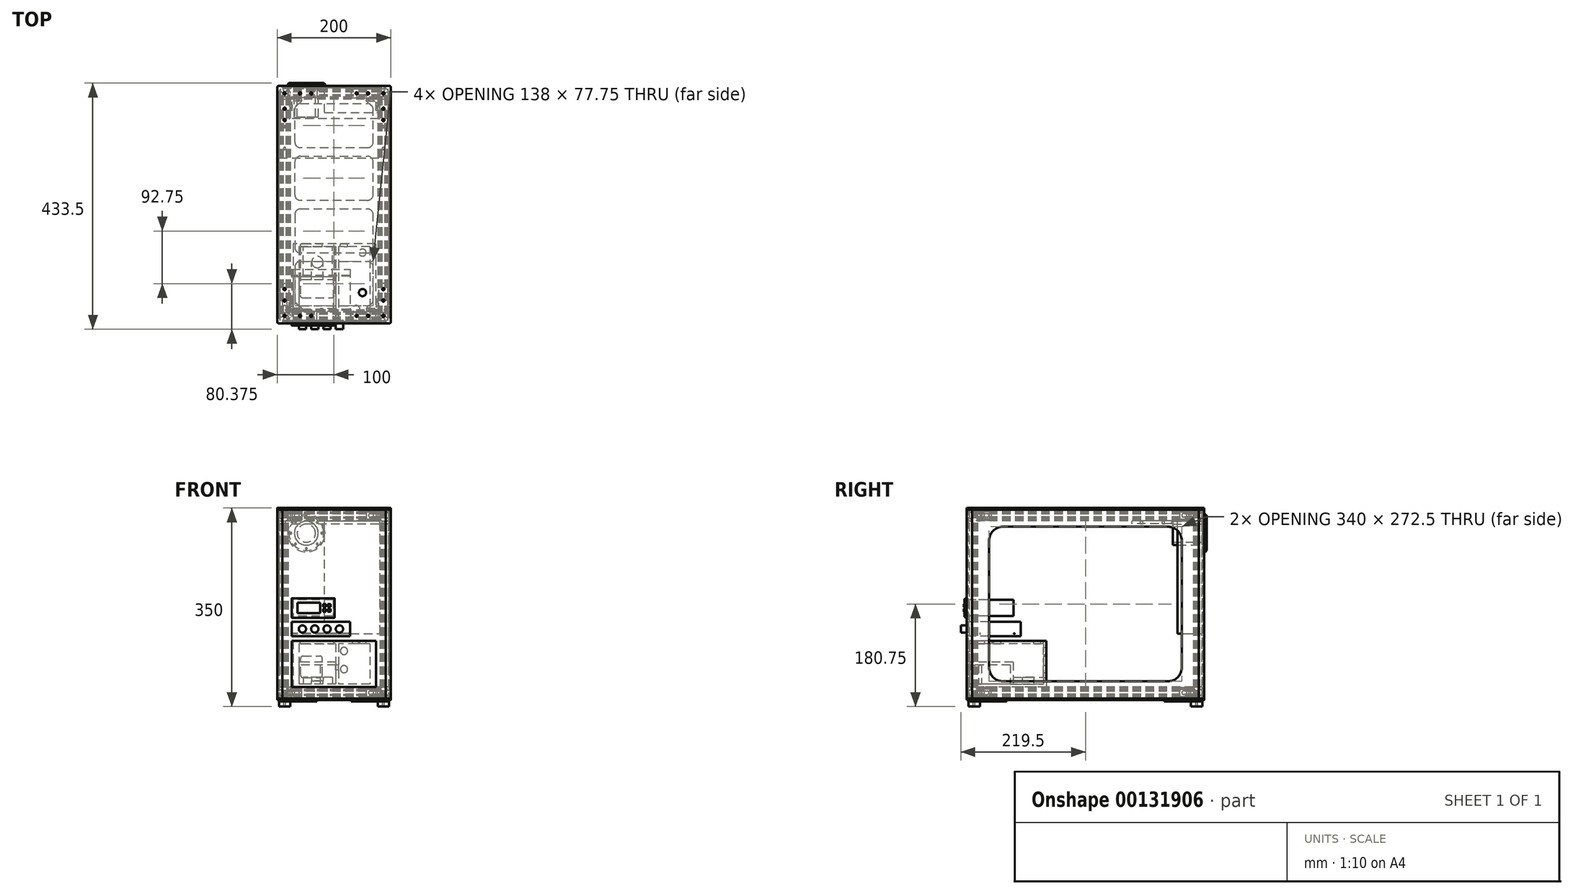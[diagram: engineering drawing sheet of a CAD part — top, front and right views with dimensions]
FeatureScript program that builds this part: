
annotation { "Feature Type Name" : "Feature", "Feature Type Description" : "" }
export const myFeature = defineFeature(function(context is Context, id is Id, definition is map)
    precondition{}
    {
        {
            var Q0;
            Q0=qCreatedBy(makeId("Front.planeOp"),FACE);
            var sketch = newSketch(context, id + "F0", { "sketchPlane" : qUnion([Q0])});
            skLineSegment(sketch, "E0.bottom", {"start": v(0, 0) * mm, "end": v(182, 0) * mm});
            skLineSegment(sketch, "E0.top", {"start": v(0, 332.5) * mm, "end": v(182, 332.5) * mm});
            skLineSegment(sketch, "E0.left", {"start": v(0, 0) * mm, "end": v(0, 332.5) * mm});
            skLineSegment(sketch, "E0.right", {"start": v(182, 0) * mm, "end": v(182, 332.5) * mm});
            skSolve(sketch);
        }
        {
            var Q0;
            Q0 = qSketchRegion(id + "F0", true);
            extrude(context, id + "F1", {"entities" : qUnion([Q0]), "oppositeDirection" : true, "depth" : 3 * mm});
        }
        {
            var Q0;
            Q0=makeQuery(id+"F1.opExtrude","SWEPT_FACE",FACE,{"disambiguationData":[OSD([sQuery(id+"F0.wireOp",EDGE,"E0.bottom")])]});
            var sketch = newSketch(context, id + "F2", { "sketchPlane" : qUnion([Q0])});
            skLineSegment(sketch, "E1.left", {"start": v(172, -3) * mm, "end": v(172, -11.56) * mm});
            skLineSegment(sketch, "E2", {"start": v(182, 0) * mm, "end": v(182, -3) * mm});
            skLineSegment(sketch, "E3", {"start": v(182, -3) * mm, "end": v(179.25, -3) * mm});
            skLineSegment(sketch, "E4", {"start": v(172, -19) * mm, "end": v(191, 0) * mm, "construction": true});
            skLineSegment(sketch, "E5", {"start": v(182, 0) * mm, "end": v(191, 0) * mm});
            skLineSegment(sketch, "E6", {"start": v(179.25, -3) * mm, "end": v(179.25, -4.5) * mm});
            skLineSegment(sketch, "E7", {"start": v(179.25, -4.5) * mm, "end": v(180.34, -4.5) * mm});
            skLineSegment(sketch, "E8", {"start": v(180.34, -4.5) * mm, "end": v(180.34, -8.25) * mm});
            skLineSegment(sketch, "E9", {"start": v(180.34, -8.25) * mm, "end": v(179.25, -8.25) * mm});
            skLineSegment(sketch, "E10", {"start": v(179.25, -8.25) * mm, "end": v(179.25, -10) * mm});
            skLineSegment(sketch, "E11", {"start": v(179.25, -10) * mm, "end": v(174.75, -10) * mm});
            skLineSegment(sketch, "E12", {"start": v(174.75, -10) * mm, "end": v(174.75, -8.25) * mm});
            skLineSegment(sketch, "E13", {"start": v(174.75, -8.25) * mm, "end": v(173.66, -8.25) * mm});
            skLineSegment(sketch, "E14", {"start": v(173.66, -8.25) * mm, "end": v(173.66, -4.5) * mm});
            skLineSegment(sketch, "E15", {"start": v(173.66, -4.5) * mm, "end": v(174.75, -4.5) * mm});
            skLineSegment(sketch, "E16", {"start": v(174.75, -4.5) * mm, "end": v(174.75, -3) * mm});
            skLineSegment(sketch, "E17", {"start": v(177, -10) * mm, "end": v(177, -3) * mm, "construction": true});
            skLineSegment(sketch, "E18.trimOffspring", {"start": v(174.75, -3) * mm, "end": v(172, -3) * mm});
            skArc(sketch, "E19", {"start": v(179.17, -11.83) * mm, "mid": v(177.27, -11.52) * mm, "end": v(176.36, -13.22) * mm});
            skArc(sketch, "E20", {"start": v(172, -11.56) * mm, "mid": v(173.6, -13.9) * mm, "end": v(176.36, -13.22) * mm});
            skLineSegment(sketch, "E21.MirrorCS", {"start": v(186.5, -16.25) * mm, "end": v(188, -16.25) * mm});
            skLineSegment(sketch, "E22.MirrorCS", {"start": v(181, -14) * mm, "end": v(188, -14) * mm, "construction": true});
            skLineSegment(sketch, "E23.MirrorCS", {"start": v(186.5, -11.75) * mm, "end": v(186.5, -10.66) * mm});
            skArc(sketch, "E24.MirrorCS", {"start": v(179.44, -19) * mm, "mid": v(177.1, -17.4) * mm, "end": v(177.78, -14.64) * mm});
            skLineSegment(sketch, "E25.MirrorCS", {"start": v(182.75, -10.66) * mm, "end": v(182.75, -11.75) * mm});
            skLineSegment(sketch, "E26.MirrorCS", {"start": v(182.75, -11.75) * mm, "end": v(181, -11.75) * mm});
            skLineSegment(sketch, "E27.MirrorCS", {"start": v(182.75, -17.34) * mm, "end": v(186.5, -17.34) * mm});
            skLineSegment(sketch, "E28.MirrorCS", {"start": v(186.5, -10.66) * mm, "end": v(182.75, -10.66) * mm});
            skLineSegment(sketch, "E29.MirrorCS", {"start": v(191, -9) * mm, "end": v(191, 0) * mm});
            skLineSegment(sketch, "E30.MirrorCS", {"start": v(181, -11.75) * mm, "end": v(181, -16.25) * mm});
            skLineSegment(sketch, "E31.MirrorCS", {"start": v(181, -16.25) * mm, "end": v(182.75, -16.25) * mm});
            skLineSegment(sketch, "E32.MirrorCS", {"start": v(188, -11.75) * mm, "end": v(186.5, -11.75) * mm});
            skLineSegment(sketch, "E33.MirrorCS", {"start": v(188, -19) * mm, "end": v(179.44, -19) * mm});
            skLineSegment(sketch, "E34.MirrorCS", {"start": v(191, -9) * mm, "end": v(188, -9) * mm});
            skLineSegment(sketch, "E35.MirrorCS", {"start": v(182.75, -16.25) * mm, "end": v(182.75, -17.34) * mm});
            skLineSegment(sketch, "E36.MirrorCS", {"start": v(188, -9) * mm, "end": v(188, -11.75) * mm});
            skLineSegment(sketch, "E37.MirrorCS", {"start": v(188, -16.25) * mm, "end": v(188, -19) * mm});
            skLineSegment(sketch, "E38.MirrorCS", {"start": v(186.5, -17.34) * mm, "end": v(186.5, -16.25) * mm});
            skArc(sketch, "E39.MirrorCS", {"start": v(179.17, -11.83) * mm, "mid": v(179.48, -13.73) * mm, "end": v(177.78, -14.64) * mm});
            skPoint(sketch, "E40.orphan", {"position": v(172, -19) * mm});
            skLineSegment(sketch, "E41.left", {"start": v(117.4, -37.11) * mm, "end": v(117.4, -45.67) * mm, "construction": true});
            skLineSegment(sketch, "E42", {"start": v(127.4, -34.11) * mm, "end": v(127.4, -37.11) * mm, "construction": true});
            skLineSegment(sketch, "E43", {"start": v(127.4, -37.11) * mm, "end": v(124.65, -37.11) * mm, "construction": true});
            skLineSegment(sketch, "E44", {"start": v(117.4, -53.11) * mm, "end": v(136.4, -34.11) * mm, "construction": true});
            skLineSegment(sketch, "E45", {"start": v(127.4, -34.11) * mm, "end": v(136.4, -34.11) * mm, "construction": true});
            skLineSegment(sketch, "E46", {"start": v(124.65, -37.11) * mm, "end": v(124.65, -38.61) * mm, "construction": true});
            skLineSegment(sketch, "E47", {"start": v(124.65, -38.61) * mm, "end": v(126.08, -38.61) * mm, "construction": true});
            skLineSegment(sketch, "E48", {"start": v(126.08, -38.61) * mm, "end": v(126.08, -42.36) * mm, "construction": true});
            skLineSegment(sketch, "E49", {"start": v(126.08, -42.36) * mm, "end": v(124.65, -42.36) * mm, "construction": true});
            skLineSegment(sketch, "E50", {"start": v(124.65, -42.36) * mm, "end": v(124.65, -44.11) * mm, "construction": true});
            skLineSegment(sketch, "E51", {"start": v(124.65, -44.11) * mm, "end": v(120.15, -44.11) * mm, "construction": true});
            skLineSegment(sketch, "E52", {"start": v(120.15, -44.11) * mm, "end": v(120.15, -42.36) * mm, "construction": true});
            skLineSegment(sketch, "E53", {"start": v(120.15, -42.36) * mm, "end": v(118.72, -42.36) * mm, "construction": true});
            skLineSegment(sketch, "E54", {"start": v(118.72, -42.36) * mm, "end": v(118.72, -38.61) * mm, "construction": true});
            skLineSegment(sketch, "E55", {"start": v(118.72, -38.61) * mm, "end": v(120.15, -38.61) * mm, "construction": true});
            skLineSegment(sketch, "E56", {"start": v(120.15, -38.61) * mm, "end": v(120.15, -37.11) * mm, "construction": true});
            skLineSegment(sketch, "E57", {"start": v(122.4, -44.11) * mm, "end": v(122.4, -37.11) * mm, "construction": true});
            skLineSegment(sketch, "E58.trimOffspring", {"start": v(120.15, -37.11) * mm, "end": v(117.4, -37.11) * mm, "construction": true});
            skArc(sketch, "E59", {"start": v(124.57, -45.95) * mm, "mid": v(122.67, -45.64) * mm, "end": v(121.76, -47.34) * mm, "construction": true});
            skArc(sketch, "E60", {"start": v(117.4, -45.67) * mm, "mid": v(119, -48) * mm, "end": v(121.76, -47.34) * mm, "construction": true});
            skLineSegment(sketch, "E61.MirrorCS", {"start": v(131.9, -50.36) * mm, "end": v(133.4, -50.36) * mm, "construction": true});
            skLineSegment(sketch, "E62.MirrorCS", {"start": v(126.4, -48.11) * mm, "end": v(133.4, -48.11) * mm, "construction": true});
            skLineSegment(sketch, "E63.MirrorCS", {"start": v(131.9, -45.86) * mm, "end": v(131.9, -44.44) * mm, "construction": true});
            skArc(sketch, "E64.MirrorCS", {"start": v(124.84, -53.11) * mm, "mid": v(122.5, -51.5) * mm, "end": v(123.18, -48.75) * mm, "construction": true});
            skLineSegment(sketch, "E65.MirrorCS", {"start": v(128.15, -44.44) * mm, "end": v(128.15, -45.86) * mm, "construction": true});
            skLineSegment(sketch, "E66.MirrorCS", {"start": v(128.15, -45.86) * mm, "end": v(126.4, -45.86) * mm, "construction": true});
            skLineSegment(sketch, "E67.MirrorCS", {"start": v(128.15, -51.8) * mm, "end": v(131.9, -51.8) * mm, "construction": true});
            skLineSegment(sketch, "E68.MirrorCS", {"start": v(131.9, -44.44) * mm, "end": v(128.15, -44.44) * mm, "construction": true});
            skLineSegment(sketch, "E69.MirrorCS", {"start": v(136.4, -43.11) * mm, "end": v(136.4, -34.11) * mm, "construction": true});
            skLineSegment(sketch, "E70.MirrorCS", {"start": v(126.4, -45.86) * mm, "end": v(126.4, -50.36) * mm, "construction": true});
            skLineSegment(sketch, "E71.MirrorCS", {"start": v(126.4, -50.36) * mm, "end": v(128.15, -50.36) * mm, "construction": true});
            skLineSegment(sketch, "E72.MirrorCS", {"start": v(133.4, -45.86) * mm, "end": v(131.9, -45.86) * mm, "construction": true});
            skLineSegment(sketch, "E73.MirrorCS", {"start": v(133.4, -53.11) * mm, "end": v(124.84, -53.11) * mm, "construction": true});
            skLineSegment(sketch, "E74.MirrorCS", {"start": v(136.4, -43.11) * mm, "end": v(133.4, -43.11) * mm, "construction": true});
            skLineSegment(sketch, "E75.MirrorCS", {"start": v(128.15, -50.36) * mm, "end": v(128.15, -51.8) * mm, "construction": true});
            skLineSegment(sketch, "E76.MirrorCS", {"start": v(133.4, -43.11) * mm, "end": v(133.4, -45.86) * mm, "construction": true});
            skLineSegment(sketch, "E77.MirrorCS", {"start": v(133.4, -50.36) * mm, "end": v(133.4, -53.11) * mm, "construction": true});
            skLineSegment(sketch, "E78.MirrorCS", {"start": v(131.9, -51.8) * mm, "end": v(131.9, -50.36) * mm, "construction": true});
            skArc(sketch, "E79.MirrorCS", {"start": v(124.57, -45.95) * mm, "mid": v(124.88, -47.85) * mm, "end": v(123.18, -48.75) * mm, "construction": true});
            skPoint(sketch, "E80.orphan", {"position": v(117.4, -53.11) * mm});
            skSolve(sketch);
        }
        {
            var Q0;
            Q0 = qSketchRegion(id + "F2", true);
            var Q1;
            Q1=makeQuery(id+"F1.opExtrude","SWEPT_FACE",FACE,{"disambiguationData":[OSD([sQuery(id+"F0.wireOp",EDGE,"E0.top")])]});
            extrude(context, id + "F3", {"entities" : qUnion([Q0]), "endBound" : BoundingType.UP_TO_SURFACE, "oppositeDirection" : true, "endBoundEntityFace" : qUnion([Q1]), "depth" : 300 * mm});
        }
        {
            var Q0;
            Q0=makeQuery(id+"F3.opExtrude","SWEPT_EDGE",EDGE,{"disambiguationData":[OSD([sQuery(id+"F2.wireOp",EDGE,"E5"),sQuery(id+"F2.wireOp",EDGE,"E29.MirrorCS")])]});
            fillet(context, id + "F4", {"entities" : qUnion([Q0]), "radius" : 2 * mm, "tangentPropagation" : true, "allowEdgeOverflow" : false});
        }
        {
            var Q0;
            Q0=makeQuery(id+"F3.opExtrude","SWEPT_FACE",FACE,{"disambiguationData":[OSD([sQuery(id+"F2.wireOp",EDGE,"E36.MirrorCS")])]});
            var sketch = newSketch(context, id + "F5", { "sketchPlane" : qUnion([Q0])});
            skPoint(sketch, "E81.0", {"position": v(9, 0) * mm});
            skLineSegment(sketch, "E82.bottom", {"start": v(9, 0) * mm, "end": v(409, 0) * mm});
            skLineSegment(sketch, "E82.top", {"start": v(9, 332.5) * mm, "end": v(409, 332.5) * mm});
            skLineSegment(sketch, "E82.left", {"start": v(9, 0) * mm, "end": v(9, 332.5) * mm});
            skLineSegment(sketch, "E82.right", {"start": v(409, 0) * mm, "end": v(409, 332.5) * mm});
            skSolve(sketch);
        }
        {
            var Q0;
            Q0 = qSketchRegion(id + "F5", true);
            extrude(context, id + "F6", {"entities" : qUnion([Q0]), "depth" : 3 * mm});
        }
        {
            var Q0;
            Q0=makeQuery(id+"F3.opExtrude","SWEPT_FACE",FACE,{"disambiguationData":[OSD([sQuery(id+"F2.wireOp",EDGE,"E33.MirrorCS")])]});
            var sketch = newSketch(context, id + "F7", { "sketchPlane" : qUnion([Q0])});
            skLineSegment(sketch, "E83.bottom", {"start": v(-186.5, 0) * mm, "end": v(-181.6, 0) * mm});
            skLineSegment(sketch, "E83.top", {"start": v(-186.5, 20) * mm, "end": v(-181.6, 20) * mm});
            skLineSegment(sketch, "E83.left", {"start": v(-188, 1.5) * mm, "end": v(-188, 6.4) * mm});
            skLineSegment(sketch, "E83.right", {"start": v(-168, 1.5) * mm, "end": v(-168, 6.4) * mm});
            skLineSegment(sketch, "E84", {"start": v(-188, 20) * mm, "end": v(-168, 0) * mm, "construction": true});
            skLineSegment(sketch, "E85", {"start": v(-168, 20) * mm, "end": v(-188, 0) * mm, "construction": true});
            skCircle(sketch, "E86", {"center": v(-178, 10) * mm, "radius": 2.5 * mm});
            skLineSegment(sketch, "E87", {"start": v(-183.5, 16.56) * mm, "end": v(-180.84, 13.9) * mm});
            skLineSegment(sketch, "E88", {"start": v(-172.5, 3.44) * mm, "end": v(-175.16, 6.1) * mm});
            skLineSegment(sketch, "E89", {"start": v(-184.56, 4.5) * mm, "end": v(-181.9, 7.16) * mm});
            skLineSegment(sketch, "E90", {"start": v(-171.44, 15.5) * mm, "end": v(-174.1, 12.84) * mm});
            skLineSegment(sketch, "E91.bottom", {"start": v(-183.5, 1.8) * mm, "end": v(-181.1, 1.8) * mm});
            skLineSegment(sketch, "E91.left", {"start": v(-186.2, 4.5) * mm, "end": v(-186.2, 6.9) * mm});
            skLineSegment(sketch, "E91.right", {"start": v(-169.8, 4.5) * mm, "end": v(-169.8, 6.9) * mm});
            skPoint(sketch, "E92.orphan", {"position": v(-169.8, 1.8) * mm});
            skPoint(sketch, "E93.orphan", {"position": v(-186.2, 1.8) * mm});
            skPoint(sketch, "E94.orphan", {"position": v(-169.8, 18.2) * mm});
            skPoint(sketch, "E95.orphan", {"position": v(-186.2, 18.2) * mm});
            skLineSegment(sketch, "E96.trimOffspring", {"start": v(-186.2, 13.1) * mm, "end": v(-186.2, 15.5) * mm});
            skLineSegment(sketch, "E97.trimOffspring", {"start": v(-169.8, 13.1) * mm, "end": v(-169.8, 15.5) * mm});
            skLineSegment(sketch, "E98.trimOffspring", {"start": v(-181.9, 12.84) * mm, "end": v(-181.9, 7.16) * mm});
            skPoint(sketch, "E99.orphan", {"position": v(-181.9, 13.9) * mm});
            skLineSegment(sketch, "E100.trimOffspring", {"start": v(-180.84, 6.1) * mm, "end": v(-175.16, 6.1) * mm});
            skPoint(sketch, "E101.orphan", {"position": v(-181.9, 6.1) * mm});
            skLineSegment(sketch, "E102.trimOffspring", {"start": v(-175.16, 13.9) * mm, "end": v(-172.5, 16.56) * mm});
            skLineSegment(sketch, "E103.trimOffspring", {"start": v(-181.9, 12.84) * mm, "end": v(-184.56, 15.5) * mm});
            skLineSegment(sketch, "E104.trimOffspring", {"start": v(-180.84, 6.1) * mm, "end": v(-183.5, 3.44) * mm});
            skLineSegment(sketch, "E105.trimOffspring", {"start": v(-174.1, 7.16) * mm, "end": v(-171.44, 4.5) * mm});
            skPoint(sketch, "E106.orphan", {"position": v(-174.1, 6.1) * mm});
            skPoint(sketch, "E107.trimOffspring.end.orphan", {"position": v(-174.1, 13.9) * mm});
            skLineSegment(sketch, "E108.trimOffspring", {"start": v(-174.1, 12.84) * mm, "end": v(-174.1, 7.16) * mm});
            skLineSegment(sketch, "E109", {"start": v(-175.16, 13.9) * mm, "end": v(-180.84, 13.9) * mm});
            skLineSegment(sketch, "E110", {"start": v(-188, 13.6) * mm, "end": v(-186.2, 13.1) * mm});
            skLineSegment(sketch, "E111", {"start": v(-188, 6.4) * mm, "end": v(-186.2, 6.9) * mm});
            skLineSegment(sketch, "E112", {"start": v(-168, 6.4) * mm, "end": v(-169.8, 6.9) * mm});
            skLineSegment(sketch, "E113", {"start": v(-169.8, 13.1) * mm, "end": v(-168, 13.6) * mm});
            skLineSegment(sketch, "E114", {"start": v(-174.4, 20) * mm, "end": v(-174.9, 18.2) * mm});
            skLineSegment(sketch, "E115", {"start": v(-181.1, 18.2) * mm, "end": v(-181.6, 20) * mm});
            skLineSegment(sketch, "E116", {"start": v(-181.1, 1.8) * mm, "end": v(-181.6, 0) * mm});
            skLineSegment(sketch, "E117", {"start": v(-174.9, 1.8) * mm, "end": v(-174.4, 0) * mm});
            skLineSegment(sketch, "E118.bottom", {"start": v(-186.2, 15.5) * mm, "end": v(-184.56, 15.5) * mm});
            skLineSegment(sketch, "E118.top", {"start": v(-186.2, 4.5) * mm, "end": v(-184.56, 4.5) * mm});
            skLineSegment(sketch, "E118.left", {"start": v(-186.2, 15.5) * mm, "end": v(-186.2, 13.1) * mm});
            skLineSegment(sketch, "E118.right", {"start": v(-169.8, 15.5) * mm, "end": v(-169.8, 13.1) * mm});
            skLineSegment(sketch, "E119.bottom", {"start": v(-183.5, 18.2) * mm, "end": v(-181.1, 18.2) * mm});
            skLineSegment(sketch, "E119.left", {"start": v(-183.5, 18.2) * mm, "end": v(-183.5, 16.56) * mm});
            skLineSegment(sketch, "E120.trimOffspring", {"start": v(-183.5, 3.44) * mm, "end": v(-183.5, 1.8) * mm});
            skLineSegment(sketch, "E121.trimOffspring", {"start": v(-174.9, 1.8) * mm, "end": v(-172.5, 1.8) * mm});
            skLineSegment(sketch, "E122.trimOffspring", {"start": v(-174.4, 0) * mm, "end": v(-169.5, 0) * mm});
            skLineSegment(sketch, "E123.trimOffspring", {"start": v(-186.2, 6.9) * mm, "end": v(-186.2, 4.5) * mm});
            skLineSegment(sketch, "E124.trimOffspring", {"start": v(-188, 13.6) * mm, "end": v(-188, 18.5) * mm});
            skLineSegment(sketch, "E125.trimOffspring", {"start": v(-169.8, 6.9) * mm, "end": v(-169.8, 4.5) * mm});
            skLineSegment(sketch, "E126.trimOffspring", {"start": v(-168, 13.6) * mm, "end": v(-168, 18.5) * mm});
            skLineSegment(sketch, "E127.trimOffspring", {"start": v(-174.9, 18.2) * mm, "end": v(-172.5, 18.2) * mm});
            skLineSegment(sketch, "E128.trimOffspring", {"start": v(-174.4, 20) * mm, "end": v(-169.5, 20) * mm});
            skLineSegment(sketch, "E129.trimOffspring", {"start": v(-171.44, 15.5) * mm, "end": v(-169.8, 15.5) * mm});
            skLineSegment(sketch, "E130.trimOffspring", {"start": v(-172.5, 3.44) * mm, "end": v(-172.5, 1.8) * mm});
            skLineSegment(sketch, "E131.trimOffspring", {"start": v(-171.44, 4.5) * mm, "end": v(-169.8, 4.5) * mm});
            skPoint(sketch, "E132.visualSharp", {"position": v(-188, 20) * mm});
            skArc(sketch, "E132.filletArc", {"start": v(-186.5, 20) * mm, "mid": v(-187.56, 19.56) * mm, "end": v(-188, 18.5) * mm});
            skPoint(sketch, "E133.visualSharp", {"position": v(-168, 20) * mm});
            skArc(sketch, "E133.filletArc", {"start": v(-168, 18.5) * mm, "mid": v(-168.44, 19.56) * mm, "end": v(-169.5, 20) * mm});
            skPoint(sketch, "E134.visualSharp", {"position": v(-168, 0) * mm});
            skArc(sketch, "E134.filletArc", {"start": v(-169.5, 0) * mm, "mid": v(-168.44, 0.44) * mm, "end": v(-168, 1.5) * mm});
            skPoint(sketch, "E135.visualSharp", {"position": v(-188, 0) * mm});
            skArc(sketch, "E135.filletArc", {"start": v(-188, 1.5) * mm, "mid": v(-187.56, 0.44) * mm, "end": v(-186.5, 0) * mm});
            skLineSegment(sketch, "E136", {"start": v(-172.5, 16.56) * mm, "end": v(-172.5, 18.2) * mm});
            skLineSegment(sketch, "E137", {"start": v(-186.2, 13.1) * mm, "end": v(-169.8, 13.1) * mm, "construction": true});
            skLineSegment(sketch, "E138", {"start": v(-169.8, 6.9) * mm, "end": v(-186.2, 6.9) * mm, "construction": true});
            skLineSegment(sketch, "E139", {"start": v(-181.1, 1.8) * mm, "end": v(-181.1, 18.2) * mm, "construction": true});
            skLineSegment(sketch, "E140", {"start": v(-174.9, 18.2) * mm, "end": v(-174.9, 1.8) * mm, "construction": true});
            skSolve(sketch);
        }
        {
            var Q0;
            Q0=makeQuery(id+"F1.opExtrude","SWEPT_FACE",FACE,{"disambiguationData":[OSD([sQuery(id+"F0.wireOp",EDGE,"E0.right")])]});
            var Q1;
            Q1=makeQuery(id+"F1.opExtrude","SWEPT_FACE",FACE,{"disambiguationData":[OSD([sQuery(id+"F0.wireOp",EDGE,"E0.left")])]});
            cPlane(context, id + "F8", {"entities" : qUnion([Q0, Q1]), "cplaneType" : CPlaneType.MID_PLANE, "offset" : 25 * mm, "width" : 150 * mm, "height" : 150 * mm});
        }
        {
            var Q0;
            Q0=makeQuery(id+"F1.opExtrude","SWEPT_FACE",FACE,{"disambiguationData":[OSD([sQuery(id+"F0.wireOp",EDGE,"E0.top")])]});
            var Q1;
            Q1=makeQuery(id+"F1.opExtrude","SWEPT_FACE",FACE,{"disambiguationData":[OSD([sQuery(id+"F0.wireOp",EDGE,"E0.bottom")])]});
            cPlane(context, id + "F9", {"entities" : qUnion([Q0, Q1]), "cplaneType" : CPlaneType.MID_PLANE, "offset" : 25 * mm, "width" : 150 * mm, "height" : 150 * mm});
        }
        {
            var Q0;
            Q0=makeQuery(id+"F6.opExtrude","SWEPT_FACE",FACE,{"disambiguationData":[OSD([sQuery(id+"F5.wireOp",EDGE,"E82.left")])]});
            var Q1;
            Q1=makeQuery(id+"F6.opExtrude","SWEPT_FACE",FACE,{"disambiguationData":[OSD([sQuery(id+"F5.wireOp",EDGE,"E82.right")])]});
            cPlane(context, id + "F10", {"entities" : qUnion([Q0, Q1]), "cplaneType" : CPlaneType.MID_PLANE, "offset" : 25 * mm, "width" : 150 * mm, "height" : 150 * mm});
        }
        {
            var Q0;
            Q0=makeQuery(id+"F3.opExtrude","SWEPT_BODY",BODY,{"disambiguationData":[OSD([sQuery(id+"F2.wireOp",EDGE,"E1.left"),sQuery(id+"F2.wireOp",EDGE,"E2"),sQuery(id+"F2.wireOp",EDGE,"E3"),sQuery(id+"F2.wireOp",EDGE,"E5"),sQuery(id+"F2.wireOp",EDGE,"E6"),sQuery(id+"F2.wireOp",EDGE,"E7"),sQuery(id+"F2.wireOp",EDGE,"E8"),sQuery(id+"F2.wireOp",EDGE,"E9"),sQuery(id+"F2.wireOp",EDGE,"E10"),sQuery(id+"F2.wireOp",EDGE,"E11"),sQuery(id+"F2.wireOp",EDGE,"E12"),sQuery(id+"F2.wireOp",EDGE,"E13"),sQuery(id+"F2.wireOp",EDGE,"E14"),sQuery(id+"F2.wireOp",EDGE,"E15"),sQuery(id+"F2.wireOp",EDGE,"E16"),sQuery(id+"F2.wireOp",EDGE,"E18.trimOffspring"),sQuery(id+"F2.wireOp",EDGE,"E19"),sQuery(id+"F2.wireOp",EDGE,"E20"),sQuery(id+"F2.wireOp",EDGE,"E21.MirrorCS"),sQuery(id+"F2.wireOp",EDGE,"E23.MirrorCS"),sQuery(id+"F2.wireOp",EDGE,"E24.MirrorCS"),sQuery(id+"F2.wireOp",EDGE,"E25.MirrorCS"),sQuery(id+"F2.wireOp",EDGE,"E26.MirrorCS"),sQuery(id+"F2.wireOp",EDGE,"E27.MirrorCS"),sQuery(id+"F2.wireOp",EDGE,"E28.MirrorCS"),sQuery(id+"F2.wireOp",EDGE,"E29.MirrorCS"),sQuery(id+"F2.wireOp",EDGE,"E30.MirrorCS"),sQuery(id+"F2.wireOp",EDGE,"E31.MirrorCS"),sQuery(id+"F2.wireOp",EDGE,"E32.MirrorCS"),sQuery(id+"F2.wireOp",EDGE,"E33.MirrorCS"),sQuery(id+"F2.wireOp",EDGE,"E34.MirrorCS"),sQuery(id+"F2.wireOp",EDGE,"E35.MirrorCS"),sQuery(id+"F2.wireOp",EDGE,"E36.MirrorCS"),sQuery(id+"F2.wireOp",EDGE,"E37.MirrorCS"),sQuery(id+"F2.wireOp",EDGE,"E38.MirrorCS"),sQuery(id+"F2.wireOp",EDGE,"E39.MirrorCS")])]});
            var Q1;
            Q1=qCreatedBy(id+"F10.planeOp",FACE);
            mirror(context, id + "F11", {"entities" : qUnion([Q0]), "mirrorPlane" : qUnion([Q1])});
        }
        {
            var Q0;
            Q0 = qSketchRegion(id + "F7", true);
            var Q1;
            Q1=makeQuery(id+"F11.opPattern","COPY",FACE,{"derivedFrom":makeQuery(id+"F3.opExtrude","SWEPT_FACE",FACE,{"disambiguationData":[OSD([sQuery(id+"F2.wireOp",EDGE,"E33.MirrorCS")])]}),"instanceName":"1"});
            extrude(context, id + "F12", {"entities" : qUnion([Q0]), "endBound" : BoundingType.UP_TO_SURFACE, "endBoundEntityFace" : qUnion([Q1]), "depth" : 25 * mm});
        }
        {
            var Q0;
            Q0=makeQuery(id+"F3.opExtrude","SWEPT_BODY",BODY,{"disambiguationData":[OSD([sQuery(id+"F2.wireOp",EDGE,"E1.left"),sQuery(id+"F2.wireOp",EDGE,"E2"),sQuery(id+"F2.wireOp",EDGE,"E3"),sQuery(id+"F2.wireOp",EDGE,"E5"),sQuery(id+"F2.wireOp",EDGE,"E6"),sQuery(id+"F2.wireOp",EDGE,"E7"),sQuery(id+"F2.wireOp",EDGE,"E8"),sQuery(id+"F2.wireOp",EDGE,"E9"),sQuery(id+"F2.wireOp",EDGE,"E10"),sQuery(id+"F2.wireOp",EDGE,"E11"),sQuery(id+"F2.wireOp",EDGE,"E12"),sQuery(id+"F2.wireOp",EDGE,"E13"),sQuery(id+"F2.wireOp",EDGE,"E14"),sQuery(id+"F2.wireOp",EDGE,"E15"),sQuery(id+"F2.wireOp",EDGE,"E16"),sQuery(id+"F2.wireOp",EDGE,"E18.trimOffspring"),sQuery(id+"F2.wireOp",EDGE,"E19"),sQuery(id+"F2.wireOp",EDGE,"E20"),sQuery(id+"F2.wireOp",EDGE,"E21.MirrorCS"),sQuery(id+"F2.wireOp",EDGE,"E23.MirrorCS"),sQuery(id+"F2.wireOp",EDGE,"E24.MirrorCS"),sQuery(id+"F2.wireOp",EDGE,"E25.MirrorCS"),sQuery(id+"F2.wireOp",EDGE,"E26.MirrorCS"),sQuery(id+"F2.wireOp",EDGE,"E27.MirrorCS"),sQuery(id+"F2.wireOp",EDGE,"E28.MirrorCS"),sQuery(id+"F2.wireOp",EDGE,"E29.MirrorCS"),sQuery(id+"F2.wireOp",EDGE,"E30.MirrorCS"),sQuery(id+"F2.wireOp",EDGE,"E31.MirrorCS"),sQuery(id+"F2.wireOp",EDGE,"E32.MirrorCS"),sQuery(id+"F2.wireOp",EDGE,"E33.MirrorCS"),sQuery(id+"F2.wireOp",EDGE,"E34.MirrorCS"),sQuery(id+"F2.wireOp",EDGE,"E35.MirrorCS"),sQuery(id+"F2.wireOp",EDGE,"E36.MirrorCS"),sQuery(id+"F2.wireOp",EDGE,"E37.MirrorCS"),sQuery(id+"F2.wireOp",EDGE,"E38.MirrorCS"),sQuery(id+"F2.wireOp",EDGE,"E39.MirrorCS")])]});
            var Q1;
            Q1=qCreatedBy(id+"F8.planeOp",FACE);
            mirror(context, id + "F13", {"entities" : qUnion([Q0]), "mirrorPlane" : qUnion([Q1])});
        }
        {
            var Q0;
            Q0=makeQuery(id+"F11.opPattern","COPY",BODY,{"derivedFrom":makeQuery(id+"F3.opExtrude","SWEPT_BODY",BODY,{"disambiguationData":[OSD([sQuery(id+"F2.wireOp",EDGE,"E1.left"),sQuery(id+"F2.wireOp",EDGE,"E2"),sQuery(id+"F2.wireOp",EDGE,"E3"),sQuery(id+"F2.wireOp",EDGE,"E5"),sQuery(id+"F2.wireOp",EDGE,"E6"),sQuery(id+"F2.wireOp",EDGE,"E7"),sQuery(id+"F2.wireOp",EDGE,"E8"),sQuery(id+"F2.wireOp",EDGE,"E9"),sQuery(id+"F2.wireOp",EDGE,"E10"),sQuery(id+"F2.wireOp",EDGE,"E11"),sQuery(id+"F2.wireOp",EDGE,"E12"),sQuery(id+"F2.wireOp",EDGE,"E13"),sQuery(id+"F2.wireOp",EDGE,"E14"),sQuery(id+"F2.wireOp",EDGE,"E15"),sQuery(id+"F2.wireOp",EDGE,"E16"),sQuery(id+"F2.wireOp",EDGE,"E18.trimOffspring"),sQuery(id+"F2.wireOp",EDGE,"E19"),sQuery(id+"F2.wireOp",EDGE,"E20"),sQuery(id+"F2.wireOp",EDGE,"E21.MirrorCS"),sQuery(id+"F2.wireOp",EDGE,"E23.MirrorCS"),sQuery(id+"F2.wireOp",EDGE,"E24.MirrorCS"),sQuery(id+"F2.wireOp",EDGE,"E25.MirrorCS"),sQuery(id+"F2.wireOp",EDGE,"E26.MirrorCS"),sQuery(id+"F2.wireOp",EDGE,"E27.MirrorCS"),sQuery(id+"F2.wireOp",EDGE,"E28.MirrorCS"),sQuery(id+"F2.wireOp",EDGE,"E29.MirrorCS"),sQuery(id+"F2.wireOp",EDGE,"E30.MirrorCS"),sQuery(id+"F2.wireOp",EDGE,"E31.MirrorCS"),sQuery(id+"F2.wireOp",EDGE,"E32.MirrorCS"),sQuery(id+"F2.wireOp",EDGE,"E33.MirrorCS"),sQuery(id+"F2.wireOp",EDGE,"E34.MirrorCS"),sQuery(id+"F2.wireOp",EDGE,"E35.MirrorCS"),sQuery(id+"F2.wireOp",EDGE,"E36.MirrorCS"),sQuery(id+"F2.wireOp",EDGE,"E37.MirrorCS"),sQuery(id+"F2.wireOp",EDGE,"E38.MirrorCS"),sQuery(id+"F2.wireOp",EDGE,"E39.MirrorCS")])]}),"instanceName":"1"});
            var Q1;
            Q1=qCreatedBy(id+"F8.planeOp",FACE);
            mirror(context, id + "F14", {"entities" : qUnion([Q0]), "mirrorPlane" : qUnion([Q1])});
        }
        {
            var Q0;
            Q0=makeQuery(id+"F6.opExtrude","SWEPT_BODY",BODY,{"disambiguationData":[OSD([sQuery(id+"F5.wireOp",EDGE,"E82.bottom"),sQuery(id+"F5.wireOp",EDGE,"E82.top"),sQuery(id+"F5.wireOp",EDGE,"E82.left"),sQuery(id+"F5.wireOp",EDGE,"E82.right")])]});
            var Q1;
            Q1=qCreatedBy(id+"F8.planeOp",FACE);
            mirror(context, id + "F15", {"entities" : qUnion([Q0]), "mirrorPlane" : qUnion([Q1])});
        }
        {
            var Q0;
            Q0=makeQuery(id+"F12.opExtrude","SWEPT_BODY",BODY,{"disambiguationData":[OSD([sQuery(id+"F7.wireOp",EDGE,"E83.bottom"),sQuery(id+"F7.wireOp",EDGE,"E83.top"),sQuery(id+"F7.wireOp",EDGE,"E83.left"),sQuery(id+"F7.wireOp",EDGE,"E83.right"),sQuery(id+"F7.wireOp",EDGE,"E86"),sQuery(id+"F7.wireOp",EDGE,"E87"),sQuery(id+"F7.wireOp",EDGE,"E88"),sQuery(id+"F7.wireOp",EDGE,"E89"),sQuery(id+"F7.wireOp",EDGE,"E90"),sQuery(id+"F7.wireOp",EDGE,"E98.trimOffspring"),sQuery(id+"F7.wireOp",EDGE,"E100.trimOffspring"),sQuery(id+"F7.wireOp",EDGE,"E102.trimOffspring"),sQuery(id+"F7.wireOp",EDGE,"E103.trimOffspring"),sQuery(id+"F7.wireOp",EDGE,"E104.trimOffspring"),sQuery(id+"F7.wireOp",EDGE,"E105.trimOffspring"),sQuery(id+"F7.wireOp",EDGE,"E108.trimOffspring"),sQuery(id+"F7.wireOp",EDGE,"E109"),sQuery(id+"F7.wireOp",EDGE,"E110"),sQuery(id+"F7.wireOp",EDGE,"E111"),sQuery(id+"F7.wireOp",EDGE,"E112"),sQuery(id+"F7.wireOp",EDGE,"E113"),sQuery(id+"F7.wireOp",EDGE,"E114"),sQuery(id+"F7.wireOp",EDGE,"E115"),sQuery(id+"F7.wireOp",EDGE,"E116"),sQuery(id+"F7.wireOp",EDGE,"E117"),sQuery(id+"F7.wireOp",EDGE,"E118.bottom"),sQuery(id+"F7.wireOp",EDGE,"E118.top"),sQuery(id+"F7.wireOp",EDGE,"E118.left"),sQuery(id+"F7.wireOp",EDGE,"E118.right"),sQuery(id+"F7.wireOp",EDGE,"E119.bottom"),sQuery(id+"F7.wireOp",EDGE,"E91.bottom"),sQuery(id+"F7.wireOp",EDGE,"E119.left"),sQuery(id+"F7.wireOp",EDGE,"E120.trimOffspring"),sQuery(id+"F7.wireOp",EDGE,"E121.trimOffspring"),sQuery(id+"F7.wireOp",EDGE,"E122.trimOffspring"),sQuery(id+"F7.wireOp",EDGE,"E123.trimOffspring"),sQuery(id+"F7.wireOp",EDGE,"E124.trimOffspring"),sQuery(id+"F7.wireOp",EDGE,"E125.trimOffspring"),sQuery(id+"F7.wireOp",EDGE,"E126.trimOffspring"),sQuery(id+"F7.wireOp",EDGE,"E128.trimOffspring"),sQuery(id+"F7.wireOp",EDGE,"E127.trimOffspring"),sQuery(id+"F7.wireOp",EDGE,"E129.trimOffspring"),sQuery(id+"F7.wireOp",EDGE,"E130.trimOffspring"),sQuery(id+"F7.wireOp",EDGE,"E131.trimOffspring"),sQuery(id+"F7.wireOp",EDGE,"E132.filletArc"),sQuery(id+"F7.wireOp",EDGE,"E133.filletArc"),sQuery(id+"F7.wireOp",EDGE,"E134.filletArc"),sQuery(id+"F7.wireOp",EDGE,"E135.filletArc"),sQuery(id+"F7.wireOp",EDGE,"E136")])]});
            var Q1;
            Q1=qCreatedBy(id+"F8.planeOp",FACE);
            mirror(context, id + "F16", {"entities" : qUnion([Q0]), "mirrorPlane" : qUnion([Q1])});
        }
        {
            var Q0;
            Q0=makeQuery(id+"F12.opExtrude","SWEPT_BODY",BODY,{"disambiguationData":[OSD([sQuery(id+"F7.wireOp",EDGE,"E83.bottom"),sQuery(id+"F7.wireOp",EDGE,"E83.top"),sQuery(id+"F7.wireOp",EDGE,"E83.left"),sQuery(id+"F7.wireOp",EDGE,"E83.right"),sQuery(id+"F7.wireOp",EDGE,"E86"),sQuery(id+"F7.wireOp",EDGE,"E87"),sQuery(id+"F7.wireOp",EDGE,"E88"),sQuery(id+"F7.wireOp",EDGE,"E89"),sQuery(id+"F7.wireOp",EDGE,"E90"),sQuery(id+"F7.wireOp",EDGE,"E98.trimOffspring"),sQuery(id+"F7.wireOp",EDGE,"E100.trimOffspring"),sQuery(id+"F7.wireOp",EDGE,"E102.trimOffspring"),sQuery(id+"F7.wireOp",EDGE,"E103.trimOffspring"),sQuery(id+"F7.wireOp",EDGE,"E104.trimOffspring"),sQuery(id+"F7.wireOp",EDGE,"E105.trimOffspring"),sQuery(id+"F7.wireOp",EDGE,"E108.trimOffspring"),sQuery(id+"F7.wireOp",EDGE,"E109"),sQuery(id+"F7.wireOp",EDGE,"E110"),sQuery(id+"F7.wireOp",EDGE,"E111"),sQuery(id+"F7.wireOp",EDGE,"E112"),sQuery(id+"F7.wireOp",EDGE,"E113"),sQuery(id+"F7.wireOp",EDGE,"E114"),sQuery(id+"F7.wireOp",EDGE,"E115"),sQuery(id+"F7.wireOp",EDGE,"E116"),sQuery(id+"F7.wireOp",EDGE,"E117"),sQuery(id+"F7.wireOp",EDGE,"E118.bottom"),sQuery(id+"F7.wireOp",EDGE,"E118.top"),sQuery(id+"F7.wireOp",EDGE,"E118.left"),sQuery(id+"F7.wireOp",EDGE,"E118.right"),sQuery(id+"F7.wireOp",EDGE,"E119.bottom"),sQuery(id+"F7.wireOp",EDGE,"E91.bottom"),sQuery(id+"F7.wireOp",EDGE,"E119.left"),sQuery(id+"F7.wireOp",EDGE,"E120.trimOffspring"),sQuery(id+"F7.wireOp",EDGE,"E121.trimOffspring"),sQuery(id+"F7.wireOp",EDGE,"E122.trimOffspring"),sQuery(id+"F7.wireOp",EDGE,"E123.trimOffspring"),sQuery(id+"F7.wireOp",EDGE,"E124.trimOffspring"),sQuery(id+"F7.wireOp",EDGE,"E125.trimOffspring"),sQuery(id+"F7.wireOp",EDGE,"E126.trimOffspring"),sQuery(id+"F7.wireOp",EDGE,"E128.trimOffspring"),sQuery(id+"F7.wireOp",EDGE,"E127.trimOffspring"),sQuery(id+"F7.wireOp",EDGE,"E129.trimOffspring"),sQuery(id+"F7.wireOp",EDGE,"E130.trimOffspring"),sQuery(id+"F7.wireOp",EDGE,"E131.trimOffspring"),sQuery(id+"F7.wireOp",EDGE,"E132.filletArc"),sQuery(id+"F7.wireOp",EDGE,"E133.filletArc"),sQuery(id+"F7.wireOp",EDGE,"E134.filletArc"),sQuery(id+"F7.wireOp",EDGE,"E135.filletArc"),sQuery(id+"F7.wireOp",EDGE,"E136")])]});
            var Q1;
            Q1=qCreatedBy(id+"F9.planeOp",FACE);
            mirror(context, id + "F17", {"entities" : qUnion([Q0]), "mirrorPlane" : qUnion([Q1])});
        }
        {
            var Q0;
            Q0=makeQuery(id+"F16.opPattern","COPY",BODY,{"derivedFrom":makeQuery(id+"F12.opExtrude","SWEPT_BODY",BODY,{"disambiguationData":[OSD([sQuery(id+"F7.wireOp",EDGE,"E83.bottom"),sQuery(id+"F7.wireOp",EDGE,"E83.top"),sQuery(id+"F7.wireOp",EDGE,"E83.left"),sQuery(id+"F7.wireOp",EDGE,"E83.right"),sQuery(id+"F7.wireOp",EDGE,"E86"),sQuery(id+"F7.wireOp",EDGE,"E87"),sQuery(id+"F7.wireOp",EDGE,"E88"),sQuery(id+"F7.wireOp",EDGE,"E89"),sQuery(id+"F7.wireOp",EDGE,"E90"),sQuery(id+"F7.wireOp",EDGE,"E98.trimOffspring"),sQuery(id+"F7.wireOp",EDGE,"E100.trimOffspring"),sQuery(id+"F7.wireOp",EDGE,"E102.trimOffspring"),sQuery(id+"F7.wireOp",EDGE,"E103.trimOffspring"),sQuery(id+"F7.wireOp",EDGE,"E104.trimOffspring"),sQuery(id+"F7.wireOp",EDGE,"E105.trimOffspring"),sQuery(id+"F7.wireOp",EDGE,"E108.trimOffspring"),sQuery(id+"F7.wireOp",EDGE,"E109"),sQuery(id+"F7.wireOp",EDGE,"E110"),sQuery(id+"F7.wireOp",EDGE,"E111"),sQuery(id+"F7.wireOp",EDGE,"E112"),sQuery(id+"F7.wireOp",EDGE,"E113"),sQuery(id+"F7.wireOp",EDGE,"E114"),sQuery(id+"F7.wireOp",EDGE,"E115"),sQuery(id+"F7.wireOp",EDGE,"E116"),sQuery(id+"F7.wireOp",EDGE,"E117"),sQuery(id+"F7.wireOp",EDGE,"E118.bottom"),sQuery(id+"F7.wireOp",EDGE,"E118.top"),sQuery(id+"F7.wireOp",EDGE,"E118.left"),sQuery(id+"F7.wireOp",EDGE,"E118.right"),sQuery(id+"F7.wireOp",EDGE,"E119.bottom"),sQuery(id+"F7.wireOp",EDGE,"E91.bottom"),sQuery(id+"F7.wireOp",EDGE,"E119.left"),sQuery(id+"F7.wireOp",EDGE,"E120.trimOffspring"),sQuery(id+"F7.wireOp",EDGE,"E121.trimOffspring"),sQuery(id+"F7.wireOp",EDGE,"E122.trimOffspring"),sQuery(id+"F7.wireOp",EDGE,"E123.trimOffspring"),sQuery(id+"F7.wireOp",EDGE,"E124.trimOffspring"),sQuery(id+"F7.wireOp",EDGE,"E125.trimOffspring"),sQuery(id+"F7.wireOp",EDGE,"E126.trimOffspring"),sQuery(id+"F7.wireOp",EDGE,"E128.trimOffspring"),sQuery(id+"F7.wireOp",EDGE,"E127.trimOffspring"),sQuery(id+"F7.wireOp",EDGE,"E129.trimOffspring"),sQuery(id+"F7.wireOp",EDGE,"E130.trimOffspring"),sQuery(id+"F7.wireOp",EDGE,"E131.trimOffspring"),sQuery(id+"F7.wireOp",EDGE,"E132.filletArc"),sQuery(id+"F7.wireOp",EDGE,"E133.filletArc"),sQuery(id+"F7.wireOp",EDGE,"E134.filletArc"),sQuery(id+"F7.wireOp",EDGE,"E135.filletArc"),sQuery(id+"F7.wireOp",EDGE,"E136")])]}),"instanceName":"1"});
            var Q1;
            Q1=qCreatedBy(id+"F9.planeOp",FACE);
            mirror(context, id + "F18", {"entities" : qUnion([Q0]), "mirrorPlane" : qUnion([Q1])});
        }
        {
            var Q0;
            Q0=makeQuery(id+"F1.opExtrude","SWEPT_BODY",BODY,{"disambiguationData":[OSD([sQuery(id+"F0.wireOp",EDGE,"E0.bottom"),sQuery(id+"F0.wireOp",EDGE,"E0.top"),sQuery(id+"F0.wireOp",EDGE,"E0.left"),sQuery(id+"F0.wireOp",EDGE,"E0.right")])]});
            var Q1;
            Q1=qCreatedBy(id+"F10.planeOp",FACE);
            mirror(context, id + "F19", {"entities" : qUnion([Q0]), "mirrorPlane" : qUnion([Q1])});
        }
        {
            var Q0;
            Q0=makeQuery(id+"F1.opExtrude","SWEPT_FACE",FACE,{"disambiguationData":[OSD([sQuery(id+"F0.wireOp",EDGE,"E0.top")])]});
            var sketch = newSketch(context, id + "F20", { "sketchPlane" : qUnion([Q0])});
            skLineSegment(sketch, "E141.bottom", {"start": v(-7, 0) * mm, "end": v(189, 0) * mm});
            skLineSegment(sketch, "E141.top", {"start": v(-7, 418) * mm, "end": v(189, 418) * mm});
            skLineSegment(sketch, "E141.left", {"start": v(-9, 2) * mm, "end": v(-9, 416) * mm});
            skLineSegment(sketch, "E141.right", {"start": v(191, 2) * mm, "end": v(191, 416) * mm});
            skPoint(sketch, "E142.visualSharp", {"position": v(-9, 418) * mm});
            skArc(sketch, "E142.filletArc", {"start": v(-7, 418) * mm, "mid": v(-8.41, 417.41) * mm, "end": v(-9, 416) * mm});
            skPoint(sketch, "E143.visualSharp", {"position": v(191, 418) * mm});
            skArc(sketch, "E143.filletArc", {"start": v(191, 416) * mm, "mid": v(190.41, 417.41) * mm, "end": v(189, 418) * mm});
            skPoint(sketch, "E144.visualSharp", {"position": v(191, 0) * mm});
            skArc(sketch, "E144.filletArc", {"start": v(189, 0) * mm, "mid": v(190.41, 0.59) * mm, "end": v(191, 2) * mm});
            skPoint(sketch, "E145.visualSharp", {"position": v(-9, 0) * mm});
            skArc(sketch, "E145.filletArc", {"start": v(-9, 2) * mm, "mid": v(-8.41, 0.59) * mm, "end": v(-7, 0) * mm});
            skArc(sketch, "E146.0", {"start": v(176.36, 13.22) * mm, "mid": v(179.17, 11.83) * mm, "end": v(177.78, 14.64) * mm, "construction": true});
            skArc(sketch, "E146.1", {"start": v(5.64, 13.22) * mm, "mid": v(2.83, 11.83) * mm, "end": v(4.22, 14.64) * mm, "construction": true});
            skArc(sketch, "E146.2", {"start": v(5.64, 404.78) * mm, "mid": v(2.83, 406.17) * mm, "end": v(4.22, 403.36) * mm, "construction": true});
            skArc(sketch, "E146.3", {"start": v(176.36, 404.78) * mm, "mid": v(179.17, 406.17) * mm, "end": v(177.78, 403.36) * mm, "construction": true});
            skLineSegment(sketch, "E147.bottom", {"start": v(178, 405) * mm, "end": v(4, 405) * mm, "construction": true});
            skLineSegment(sketch, "E147.top", {"start": v(178, 13) * mm, "end": v(4, 13) * mm, "construction": true});
            skLineSegment(sketch, "E147.left", {"start": v(178, 405) * mm, "end": v(178, 13) * mm, "construction": true});
            skLineSegment(sketch, "E147.right", {"start": v(4, 405) * mm, "end": v(4, 13) * mm, "construction": true});
            skCircle(sketch, "E148", {"center": v(4, 13) * mm, "radius": 2 * mm});
            skCircle(sketch, "E149", {"center": v(178, 13) * mm, "radius": 2 * mm});
            skCircle(sketch, "E150", {"center": v(178, 405) * mm, "radius": 2 * mm});
            skCircle(sketch, "E151", {"center": v(4, 405) * mm, "radius": 2 * mm});
            skCircle(sketch, "E152", {"center": v(31, 405) * mm, "radius": 2 * mm});
            skCircle(sketch, "E153", {"center": v(151, 405) * mm, "radius": 2 * mm});
            skCircle(sketch, "E154", {"center": v(178, 378) * mm, "radius": 2 * mm});
            skCircle(sketch, "E155", {"center": v(178, 358) * mm, "radius": 2 * mm});
            skCircle(sketch, "E156", {"center": v(4, 378) * mm, "radius": 2 * mm});
            skCircle(sketch, "E157", {"center": v(4, 358) * mm, "radius": 2 * mm});
            skCircle(sketch, "E158", {"center": v(4, 40) * mm, "radius": 2 * mm});
            skCircle(sketch, "E159", {"center": v(4, 60) * mm, "radius": 2 * mm});
            skCircle(sketch, "E160", {"center": v(178, 60) * mm, "radius": 2 * mm});
            skCircle(sketch, "E161", {"center": v(178, 40) * mm, "radius": 2 * mm});
            skCircle(sketch, "E162", {"center": v(151, 13) * mm, "radius": 2 * mm});
            skCircle(sketch, "E163", {"center": v(131, 13) * mm, "radius": 2 * mm});
            skCircle(sketch, "E164", {"center": v(31, 13) * mm, "radius": 2 * mm});
            skCircle(sketch, "E165", {"center": v(51, 13) * mm, "radius": 2 * mm});
            skLineSegment(sketch, "E166", {"start": v(4, 378) * mm, "end": v(178, 378) * mm, "construction": true});
            skLineSegment(sketch, "E167", {"start": v(4, 358) * mm, "end": v(178, 358) * mm, "construction": true});
            skLineSegment(sketch, "E168", {"start": v(4, 60) * mm, "end": v(178, 60) * mm, "construction": true});
            skLineSegment(sketch, "E169", {"start": v(4, 40) * mm, "end": v(178, 40) * mm, "construction": true});
            skLineSegment(sketch, "E170", {"start": v(31, 13) * mm, "end": v(31, 405) * mm, "construction": true});
            skLineSegment(sketch, "E171", {"start": v(151, 13) * mm, "end": v(151, 405) * mm, "construction": true});
            skCircle(sketch, "E172", {"center": v(51, 405) * mm, "radius": 2 * mm});
            skCircle(sketch, "E173", {"center": v(131, 405) * mm, "radius": 2 * mm});
            skLineSegment(sketch, "E174", {"start": v(51, 405) * mm, "end": v(51, 13) * mm, "construction": true});
            skLineSegment(sketch, "E175", {"start": v(131, 405) * mm, "end": v(131, 13) * mm, "construction": true});
            skSolve(sketch);
        }
        {
            var Q0;
            Q0 = qSketchRegion(id + "F20", true);
            extrude(context, id + "F21", {"entities" : qUnion([Q0]), "depth" : 3 * mm});
        }
        {
            var Q0;
            Q0=makeQuery(id+"F21.opExtrude","SWEPT_BODY",BODY,{"disambiguationData":[OSD([sQuery(id+"F20.wireOp",EDGE,"E141.bottom"),sQuery(id+"F20.wireOp",EDGE,"E141.top"),sQuery(id+"F20.wireOp",EDGE,"E141.left"),sQuery(id+"F20.wireOp",EDGE,"E141.right"),sQuery(id+"F20.wireOp",EDGE,"E142.filletArc"),sQuery(id+"F20.wireOp",EDGE,"E143.filletArc"),sQuery(id+"F20.wireOp",EDGE,"E144.filletArc"),sQuery(id+"F20.wireOp",EDGE,"E145.filletArc"),sQuery(id+"F20.wireOp",EDGE,"E148"),sQuery(id+"F20.wireOp",EDGE,"E149"),sQuery(id+"F20.wireOp",EDGE,"E150"),sQuery(id+"F20.wireOp",EDGE,"E151"),sQuery(id+"F20.wireOp",EDGE,"E152"),sQuery(id+"F20.wireOp",EDGE,"E153"),sQuery(id+"F20.wireOp",EDGE,"E154"),sQuery(id+"F20.wireOp",EDGE,"E155"),sQuery(id+"F20.wireOp",EDGE,"E156"),sQuery(id+"F20.wireOp",EDGE,"E157"),sQuery(id+"F20.wireOp",EDGE,"E158"),sQuery(id+"F20.wireOp",EDGE,"E159"),sQuery(id+"F20.wireOp",EDGE,"E160"),sQuery(id+"F20.wireOp",EDGE,"E161"),sQuery(id+"F20.wireOp",EDGE,"E162"),sQuery(id+"F20.wireOp",EDGE,"E163"),sQuery(id+"F20.wireOp",EDGE,"E164"),sQuery(id+"F20.wireOp",EDGE,"E165"),sQuery(id+"F20.wireOp",EDGE,"E172"),sQuery(id+"F20.wireOp",EDGE,"E173")])]});
            var Q1;
            Q1=qCreatedBy(id+"F9.planeOp",FACE);
            mirror(context, id + "F22", {"entities" : qUnion([Q0]), "mirrorPlane" : qUnion([Q1])});
        }
        {
            var Q0;
            Q0=makeQuery(id+"F22.opPattern","COPY",FACE,{"derivedFrom":makeQuery(id+"F21.opExtrude","CAP_FACE",FACE,{"disambiguationData":[OSD([sQuery(id+"F20.wireOp",EDGE,"E141.bottom"),sQuery(id+"F20.wireOp",EDGE,"E141.top"),sQuery(id+"F20.wireOp",EDGE,"E141.left"),sQuery(id+"F20.wireOp",EDGE,"E141.right"),sQuery(id+"F20.wireOp",EDGE,"E142.filletArc"),sQuery(id+"F20.wireOp",EDGE,"E143.filletArc"),sQuery(id+"F20.wireOp",EDGE,"E144.filletArc"),sQuery(id+"F20.wireOp",EDGE,"E145.filletArc"),sQuery(id+"F20.wireOp",EDGE,"E148"),sQuery(id+"F20.wireOp",EDGE,"E149"),sQuery(id+"F20.wireOp",EDGE,"E150"),sQuery(id+"F20.wireOp",EDGE,"E151"),sQuery(id+"F20.wireOp",EDGE,"E152"),sQuery(id+"F20.wireOp",EDGE,"E153"),sQuery(id+"F20.wireOp",EDGE,"E154"),sQuery(id+"F20.wireOp",EDGE,"E155"),sQuery(id+"F20.wireOp",EDGE,"E156"),sQuery(id+"F20.wireOp",EDGE,"E157"),sQuery(id+"F20.wireOp",EDGE,"E158"),sQuery(id+"F20.wireOp",EDGE,"E159"),sQuery(id+"F20.wireOp",EDGE,"E160"),sQuery(id+"F20.wireOp",EDGE,"E161"),sQuery(id+"F20.wireOp",EDGE,"E162"),sQuery(id+"F20.wireOp",EDGE,"E163"),sQuery(id+"F20.wireOp",EDGE,"E164"),sQuery(id+"F20.wireOp",EDGE,"E165"),sQuery(id+"F20.wireOp",EDGE,"E172"),sQuery(id+"F20.wireOp",EDGE,"E173")])],"isStart":false}),"instanceName":"1"});
            var sketch = newSketch(context, id + "F23", { "sketchPlane" : qUnion([Q0])});
            skLineSegment(sketch, "E176.bottom", {"start": v(121, -5) * mm, "end": v(186, -5) * mm});
            skLineSegment(sketch, "E176.top", {"start": v(121, -21) * mm, "end": v(170, -21) * mm});
            skLineSegment(sketch, "E176.left", {"start": v(121, -5) * mm, "end": v(121, -21) * mm});
            skLineSegment(sketch, "E176.right", {"start": v(186, -5) * mm, "end": v(186, -21) * mm});
            skLineSegment(sketch, "E177.top", {"start": v(186, -70) * mm, "end": v(170, -70) * mm});
            skLineSegment(sketch, "E177.left", {"start": v(186, -21) * mm, "end": v(186, -70) * mm});
            skLineSegment(sketch, "E177.right", {"start": v(170, -21) * mm, "end": v(170, -70) * mm});
            skCircle(sketch, "E178.0", {"center": v(178, -13) * mm, "radius": 2 * mm});
            skCircle(sketch, "E178.1", {"center": v(151, -13) * mm, "radius": 2 * mm});
            skCircle(sketch, "E178.2", {"center": v(131, -13) * mm, "radius": 2 * mm});
            skCircle(sketch, "E178.3", {"center": v(178, -40) * mm, "radius": 2 * mm});
            skCircle(sketch, "E178.4", {"center": v(178, -60) * mm, "radius": 2 * mm});
            skSolve(sketch);
        }
        {
            var Q0;
            Q0 = qSketchRegion(id + "F23", true);
            extrude(context, id + "F24", {"entities" : qUnion([Q0]), "depth" : 2.5 * mm});
        }
        {
            var Q0;
            Q0=makeQuery(id+"F24.opExtrude","SWEPT_BODY",BODY,{"disambiguationData":[OSD([sQuery(id+"F23.wireOp",EDGE,"E176.bottom"),sQuery(id+"F23.wireOp",EDGE,"E176.top"),sQuery(id+"F23.wireOp",EDGE,"E176.left"),sQuery(id+"F23.wireOp",EDGE,"E176.right"),sQuery(id+"F23.wireOp",EDGE,"E177.top"),sQuery(id+"F23.wireOp",EDGE,"E177.left"),sQuery(id+"F23.wireOp",EDGE,"E177.right"),sQuery(id+"F23.wireOp",EDGE,"E178.0"),sQuery(id+"F23.wireOp",EDGE,"E178.1"),sQuery(id+"F23.wireOp",EDGE,"E178.2"),sQuery(id+"F23.wireOp",EDGE,"E178.3"),sQuery(id+"F23.wireOp",EDGE,"E178.4")])]});
            var Q1;
            Q1=qCreatedBy(id+"F8.planeOp",FACE);
            mirror(context, id + "F25", {"entities" : qUnion([Q0]), "mirrorPlane" : qUnion([Q1])});
        }
        {
            var Q0;
            Q0=makeQuery(id+"F24.opExtrude","SWEPT_BODY",BODY,{"disambiguationData":[OSD([sQuery(id+"F23.wireOp",EDGE,"E176.bottom"),sQuery(id+"F23.wireOp",EDGE,"E176.top"),sQuery(id+"F23.wireOp",EDGE,"E176.left"),sQuery(id+"F23.wireOp",EDGE,"E176.right"),sQuery(id+"F23.wireOp",EDGE,"E177.top"),sQuery(id+"F23.wireOp",EDGE,"E177.left"),sQuery(id+"F23.wireOp",EDGE,"E177.right"),sQuery(id+"F23.wireOp",EDGE,"E178.0"),sQuery(id+"F23.wireOp",EDGE,"E178.1"),sQuery(id+"F23.wireOp",EDGE,"E178.2"),sQuery(id+"F23.wireOp",EDGE,"E178.3"),sQuery(id+"F23.wireOp",EDGE,"E178.4")])]});
            var Q1;
            Q1=qCreatedBy(id+"F10.planeOp",FACE);
            mirror(context, id + "F26", {"entities" : qUnion([Q0]), "mirrorPlane" : qUnion([Q1])});
        }
        {
            var Q0;
            Q0=makeQuery(id+"F26.opPattern","COPY",BODY,{"derivedFrom":makeQuery(id+"F24.opExtrude","SWEPT_BODY",BODY,{"disambiguationData":[OSD([sQuery(id+"F23.wireOp",EDGE,"E176.bottom"),sQuery(id+"F23.wireOp",EDGE,"E176.top"),sQuery(id+"F23.wireOp",EDGE,"E176.left"),sQuery(id+"F23.wireOp",EDGE,"E176.right"),sQuery(id+"F23.wireOp",EDGE,"E177.top"),sQuery(id+"F23.wireOp",EDGE,"E177.left"),sQuery(id+"F23.wireOp",EDGE,"E177.right"),sQuery(id+"F23.wireOp",EDGE,"E178.0"),sQuery(id+"F23.wireOp",EDGE,"E178.1"),sQuery(id+"F23.wireOp",EDGE,"E178.2"),sQuery(id+"F23.wireOp",EDGE,"E178.3"),sQuery(id+"F23.wireOp",EDGE,"E178.4")])]}),"instanceName":"1"});
            var Q1;
            Q1=qCreatedBy(id+"F8.planeOp",FACE);
            mirror(context, id + "F27", {"entities" : qUnion([Q0]), "mirrorPlane" : qUnion([Q1])});
        }
        {
            var Q0;
            Q0=makeQuery(id+"F24.opExtrude","CAP_FACE",FACE,{"disambiguationData":[OSD([sQuery(id+"F23.wireOp",EDGE,"E176.bottom"),sQuery(id+"F23.wireOp",EDGE,"E176.top"),sQuery(id+"F23.wireOp",EDGE,"E176.left"),sQuery(id+"F23.wireOp",EDGE,"E176.right"),sQuery(id+"F23.wireOp",EDGE,"E177.top"),sQuery(id+"F23.wireOp",EDGE,"E177.left"),sQuery(id+"F23.wireOp",EDGE,"E177.right"),sQuery(id+"F23.wireOp",EDGE,"E178.0"),sQuery(id+"F23.wireOp",EDGE,"E178.1"),sQuery(id+"F23.wireOp",EDGE,"E178.2"),sQuery(id+"F23.wireOp",EDGE,"E178.3"),sQuery(id+"F23.wireOp",EDGE,"E178.4")])],"isStart":false});
            var sketch = newSketch(context, id + "F28", { "sketchPlane" : qUnion([Q0])});
            skCircle(sketch, "E179", {"center": v(178, -13) * mm, "radius": 10 * mm});
            skCircle(sketch, "E180", {"center": v(178, -13) * mm, "radius": 1.6 * mm});
            skSolve(sketch);
        }
        {
            var Q0;
            Q0 = qSketchRegion(id + "F28", true);
            extrude(context, id + "F29", {"entities" : qUnion([Q0]), "depth" : 9 * mm});
        }
        {
            var Q0;
            Q0=makeQuery(id+"F29.opExtrude","SWEPT_BODY",BODY,{"disambiguationData":[OSD([sQuery(id+"F28.wireOp",EDGE,"E179"),sQuery(id+"F28.wireOp",EDGE,"E180")])]});
            var Q1;
            Q1=qCreatedBy(id+"F10.planeOp",FACE);
            mirror(context, id + "F30", {"entities" : qUnion([Q0]), "mirrorPlane" : qUnion([Q1])});
        }
        {
            var Q0;
            Q0=makeQuery(id+"F29.opExtrude","SWEPT_BODY",BODY,{"disambiguationData":[OSD([sQuery(id+"F28.wireOp",EDGE,"E179"),sQuery(id+"F28.wireOp",EDGE,"E180")])]});
            var Q1;
            Q1=qCreatedBy(id+"F8.planeOp",FACE);
            mirror(context, id + "F31", {"entities" : qUnion([Q0]), "mirrorPlane" : qUnion([Q1])});
        }
        {
            var Q0;
            {var subQ2=sQuery(id+"F5.wireOp",EDGE,"E82.right");Q0=makeQuery(id+"F5.imprint","IMPRINT",FACE,{"disambiguationData":[TD([[makeQuery(id+"F5.imprint","IMPRINT",EDGE,{"derivedFrom":subQ2}),1.0]])]});}
            var sketch = newSketch(context, id + "F32", { "sketchPlane" : qUnion([Q0])});
            skLineSegment(sketch, "E181.bottom", {"start": v(64, 302.5) * mm, "end": v(354, 302.5) * mm});
            skLineSegment(sketch, "E181.top", {"start": v(64, 30) * mm, "end": v(354, 30) * mm});
            skLineSegment(sketch, "E182", {"start": v(39, 277.5) * mm, "end": v(39, 55) * mm});
            skLineSegment(sketch, "E183", {"start": v(379, 55) * mm, "end": v(379, 277.5) * mm});
            skPoint(sketch, "E184.visualSharp", {"position": v(39, 302.5) * mm});
            skArc(sketch, "E184.filletArc", {"start": v(64, 302.5) * mm, "mid": v(46.32, 295.18) * mm, "end": v(39, 277.5) * mm});
            skPoint(sketch, "E185.visualSharp", {"position": v(39, 30) * mm});
            skArc(sketch, "E185.filletArc", {"start": v(39, 55) * mm, "mid": v(46.32, 37.32) * mm, "end": v(64, 30) * mm});
            skPoint(sketch, "E186.visualSharp", {"position": v(379, 30) * mm});
            skArc(sketch, "E186.filletArc", {"start": v(354, 30) * mm, "mid": v(371.68, 37.32) * mm, "end": v(379, 55) * mm});
            skPoint(sketch, "E187.visualSharp", {"position": v(379, 302.5) * mm});
            skArc(sketch, "E187.filletArc", {"start": v(379, 277.5) * mm, "mid": v(371.68, 295.18) * mm, "end": v(354, 302.5) * mm});
            skSolve(sketch);
        }
        {
            var Q0;
            Q0=makeQuery(id+"F30.opPattern","COPY",BODY,{"derivedFrom":makeQuery(id+"F29.opExtrude","SWEPT_BODY",BODY,{"disambiguationData":[OSD([sQuery(id+"F28.wireOp",EDGE,"E179"),sQuery(id+"F28.wireOp",EDGE,"E180")])]}),"instanceName":"1"});
            var Q1;
            Q1=qCreatedBy(id+"F8.planeOp",FACE);
            mirror(context, id + "F33", {"entities" : qUnion([Q0]), "mirrorPlane" : qUnion([Q1])});
        }
        {
            var Q0;
            Q0 = qSketchRegion(id + "F32", true);
            extrude(context, id + "F34", {"entities" : qUnion([Q0]), "operationType" : NewBodyOperationType.REMOVE, "endBound" : BoundingType.THROUGH_ALL, "depth" : 25 * mm, "hasSecondDirection" : true, "secondDirectionBound" : SecondDirectionBoundingType.THROUGH_ALL, "secondDirectionOppositeDirection" : true, "secondDirectionDepth" : 25 * mm});
        }
        {
            var Q0;
            Q0=makeQuery(id+"F13.opPattern","COPY",FACE,{"derivedFrom":makeQuery(id+"F3.opExtrude","SWEPT_FACE",FACE,{"disambiguationData":[OSD([sQuery(id+"F2.wireOp",EDGE,"E1.left")])]}),"instanceName":"1"});
            var sketch = newSketch(context, id + "F35", { "sketchPlane" : qUnion([Q0])});
            skLineSegment(sketch, "E188.bottom", {"start": v(4.5, 312.5) * mm, "end": v(9.4, 312.5) * mm});
            skLineSegment(sketch, "E188.top", {"start": v(4.5, 332.5) * mm, "end": v(9.4, 332.5) * mm});
            skLineSegment(sketch, "E188.left", {"start": v(3, 314) * mm, "end": v(3, 318.9) * mm});
            skLineSegment(sketch, "E188.right", {"start": v(23, 314) * mm, "end": v(23, 318.9) * mm});
            skLineSegment(sketch, "E189", {"start": v(3, 332.5) * mm, "end": v(23, 312.5) * mm, "construction": true});
            skLineSegment(sketch, "E190", {"start": v(23, 332.5) * mm, "end": v(3, 312.5) * mm, "construction": true});
            skCircle(sketch, "E191", {"center": v(13, 322.5) * mm, "radius": 2.5 * mm});
            skLineSegment(sketch, "E192", {"start": v(7.5, 329.06) * mm, "end": v(10.16, 326.4) * mm});
            skLineSegment(sketch, "E193", {"start": v(18.5, 315.94) * mm, "end": v(15.84, 318.6) * mm});
            skLineSegment(sketch, "E194", {"start": v(6.44, 317) * mm, "end": v(9.1, 319.66) * mm});
            skLineSegment(sketch, "E195", {"start": v(19.56, 328) * mm, "end": v(16.9, 325.34) * mm});
            skLineSegment(sketch, "E196.bottom", {"start": v(7.5, 314.3) * mm, "end": v(9.9, 314.3) * mm});
            skLineSegment(sketch, "E196.left", {"start": v(4.8, 317) * mm, "end": v(4.8, 319.4) * mm});
            skLineSegment(sketch, "E196.right", {"start": v(21.2, 317) * mm, "end": v(21.2, 319.4) * mm});
            skPoint(sketch, "E197.orphan", {"position": v(21.2, 314.3) * mm});
            skPoint(sketch, "E198.orphan", {"position": v(4.8, 314.3) * mm});
            skPoint(sketch, "E199.orphan", {"position": v(21.2, 330.7) * mm});
            skPoint(sketch, "E200.orphan", {"position": v(4.8, 330.7) * mm});
            skLineSegment(sketch, "E201.trimOffspring", {"start": v(4.8, 325.6) * mm, "end": v(4.8, 328) * mm});
            skLineSegment(sketch, "E202.trimOffspring", {"start": v(21.2, 325.6) * mm, "end": v(21.2, 328) * mm});
            skLineSegment(sketch, "E203.trimOffspring", {"start": v(9.1, 325.34) * mm, "end": v(9.1, 319.66) * mm});
            skPoint(sketch, "E204.orphan", {"position": v(9.1, 326.4) * mm});
            skLineSegment(sketch, "E205.trimOffspring", {"start": v(10.16, 318.6) * mm, "end": v(15.84, 318.6) * mm});
            skPoint(sketch, "E206.orphan", {"position": v(-67.09, 242.41) * mm});
            skLineSegment(sketch, "E207.trimOffspring", {"start": v(15.84, 326.4) * mm, "end": v(18.5, 329.06) * mm});
            skLineSegment(sketch, "E208.trimOffspring", {"start": v(9.1, 325.34) * mm, "end": v(6.44, 328) * mm});
            skLineSegment(sketch, "E209.trimOffspring", {"start": v(10.16, 318.6) * mm, "end": v(7.5, 315.94) * mm});
            skLineSegment(sketch, "E210.trimOffspring", {"start": v(16.9, 319.66) * mm, "end": v(19.56, 317) * mm});
            skPoint(sketch, "E211.orphan", {"position": v(16.9, 318.6) * mm});
            skPoint(sketch, "E212.trimOffspring.end.orphan", {"position": v(93.09, 402.59) * mm});
            skLineSegment(sketch, "E213.trimOffspring", {"start": v(16.9, 325.34) * mm, "end": v(16.9, 319.66) * mm});
            skLineSegment(sketch, "E214", {"start": v(15.84, 326.4) * mm, "end": v(10.16, 326.4) * mm});
            skLineSegment(sketch, "E215", {"start": v(3, 326.1) * mm, "end": v(4.8, 325.6) * mm});
            skLineSegment(sketch, "E216", {"start": v(3, 318.9) * mm, "end": v(4.8, 319.4) * mm});
            skLineSegment(sketch, "E217", {"start": v(23, 318.9) * mm, "end": v(21.2, 319.4) * mm});
            skLineSegment(sketch, "E218", {"start": v(21.2, 325.6) * mm, "end": v(23, 326.1) * mm});
            skLineSegment(sketch, "E219", {"start": v(16.6, 332.5) * mm, "end": v(16.1, 330.7) * mm});
            skLineSegment(sketch, "E220", {"start": v(9.9, 330.7) * mm, "end": v(9.4, 332.5) * mm});
            skLineSegment(sketch, "E221", {"start": v(9.9, 314.3) * mm, "end": v(9.4, 312.5) * mm});
            skLineSegment(sketch, "E222", {"start": v(16.1, 314.3) * mm, "end": v(16.6, 312.5) * mm});
            skLineSegment(sketch, "E223.bottom", {"start": v(4.8, 328) * mm, "end": v(6.44, 328) * mm});
            skLineSegment(sketch, "E223.top", {"start": v(4.8, 317) * mm, "end": v(6.44, 317) * mm});
            skLineSegment(sketch, "E223.left", {"start": v(4.8, 328) * mm, "end": v(4.8, 325.6) * mm});
            skLineSegment(sketch, "E223.right", {"start": v(21.2, 328) * mm, "end": v(21.2, 325.6) * mm});
            skLineSegment(sketch, "E224.bottom", {"start": v(7.5, 330.7) * mm, "end": v(9.9, 330.7) * mm});
            skLineSegment(sketch, "E224.left", {"start": v(7.5, 330.7) * mm, "end": v(7.5, 329.06) * mm});
            skLineSegment(sketch, "E225.trimOffspring", {"start": v(7.5, 315.94) * mm, "end": v(7.5, 314.3) * mm});
            skLineSegment(sketch, "E226.trimOffspring", {"start": v(16.1, 314.3) * mm, "end": v(18.5, 314.3) * mm});
            skLineSegment(sketch, "E227.trimOffspring", {"start": v(16.6, 312.5) * mm, "end": v(21.5, 312.5) * mm});
            skLineSegment(sketch, "E228.trimOffspring", {"start": v(4.8, 319.4) * mm, "end": v(4.8, 317) * mm});
            skLineSegment(sketch, "E229.trimOffspring", {"start": v(3, 326.1) * mm, "end": v(3, 331) * mm});
            skLineSegment(sketch, "E230.trimOffspring", {"start": v(21.2, 319.4) * mm, "end": v(21.2, 317) * mm});
            skLineSegment(sketch, "E231.trimOffspring", {"start": v(23, 326.1) * mm, "end": v(23, 331) * mm});
            skLineSegment(sketch, "E232.trimOffspring", {"start": v(16.1, 330.7) * mm, "end": v(18.5, 330.7) * mm});
            skLineSegment(sketch, "E233.trimOffspring", {"start": v(16.6, 332.5) * mm, "end": v(21.5, 332.5) * mm});
            skLineSegment(sketch, "E234.trimOffspring", {"start": v(19.56, 328) * mm, "end": v(21.2, 328) * mm});
            skLineSegment(sketch, "E235.trimOffspring", {"start": v(18.5, 315.94) * mm, "end": v(18.5, 314.3) * mm});
            skLineSegment(sketch, "E236.trimOffspring", {"start": v(19.56, 317) * mm, "end": v(21.2, 317) * mm});
            skPoint(sketch, "E237.visualSharp", {"position": v(3, 332.5) * mm});
            skArc(sketch, "E237.filletArc", {"start": v(4.5, 332.5) * mm, "mid": v(3.44, 332.06) * mm, "end": v(3, 331) * mm});
            skPoint(sketch, "E238.visualSharp", {"position": v(23, 332.5) * mm});
            skArc(sketch, "E238.filletArc", {"start": v(23, 331) * mm, "mid": v(22.56, 332.06) * mm, "end": v(21.5, 332.5) * mm});
            skPoint(sketch, "E239.visualSharp", {"position": v(23, 312.5) * mm});
            skArc(sketch, "E239.filletArc", {"start": v(21.5, 312.5) * mm, "mid": v(22.56, 312.94) * mm, "end": v(23, 314) * mm});
            skPoint(sketch, "E240.visualSharp", {"position": v(3, 312.5) * mm});
            skArc(sketch, "E240.filletArc", {"start": v(3, 314) * mm, "mid": v(3.44, 312.94) * mm, "end": v(4.5, 312.5) * mm});
            skLineSegment(sketch, "E241", {"start": v(18.5, 329.06) * mm, "end": v(18.5, 330.7) * mm});
            skLineSegment(sketch, "E242", {"start": v(4.8, 325.6) * mm, "end": v(21.2, 325.6) * mm, "construction": true});
            skLineSegment(sketch, "E243", {"start": v(21.2, 319.4) * mm, "end": v(4.8, 319.4) * mm, "construction": true});
            skLineSegment(sketch, "E244", {"start": v(9.9, 314.3) * mm, "end": v(9.9, 330.7) * mm, "construction": true});
            skLineSegment(sketch, "E245", {"start": v(16.1, 330.7) * mm, "end": v(16.1, 314.3) * mm, "construction": true});
            skSolve(sketch);
        }
        {
            var Q0;
            Q0 = qSketchRegion(id + "F35", true);
            var Q1;
            Q1=makeQuery(id+"F3.opExtrude","SWEPT_FACE",FACE,{"disambiguationData":[OSD([sQuery(id+"F2.wireOp",EDGE,"E1.left")])]});
            extrude(context, id + "F36", {"entities" : qUnion([Q0]), "endBound" : BoundingType.UP_TO_SURFACE, "endBoundEntityFace" : qUnion([Q1]), "depth" : 25 * mm});
        }
        {
            var Q0;
            Q0=makeQuery(id+"F36.opExtrude","SWEPT_FACE",FACE,{"disambiguationData":[OSD([sQuery(id+"F35.wireOp",EDGE,"E233.trimOffspring")])]});
            var sketch = newSketch(context, id + "F37", { "sketchPlane" : qUnion([Q0])});
            skLineSegment(sketch, "E246.bottom", {"start": v(10, 19.05) * mm, "end": v(14, 19.05) * mm});
            skLineSegment(sketch, "E246.top", {"start": v(10, 23) * mm, "end": v(14, 23) * mm});
            skLineSegment(sketch, "E246.left", {"start": v(10, 19.05) * mm, "end": v(10, 23) * mm});
            skLineSegment(sketch, "E246.right", {"start": v(14, 19.05) * mm, "end": v(14, 23) * mm});
            skLineSegment(sketch, "E247", {"start": v(91, 21.5) * mm, "end": v(91, 16.6) * mm, "construction": true});
            skLineSegment(sketch, "E248.MirrorCS", {"start": v(172, 19.05) * mm, "end": v(172, 23) * mm});
            skLineSegment(sketch, "E249.MirrorCS", {"start": v(172, 23) * mm, "end": v(168, 23) * mm});
            skLineSegment(sketch, "E250.MirrorCS", {"start": v(172, 19.05) * mm, "end": v(168, 19.05) * mm});
            skLineSegment(sketch, "E251.MirrorCS", {"start": v(168, 19.05) * mm, "end": v(168, 23) * mm});
            skSolve(sketch);
        }
        {
            var Q0;
            Q0 = qSketchRegion(id + "F37", true);
            extrude(context, id + "F38", {"entities" : qUnion([Q0]), "operationType" : NewBodyOperationType.REMOVE, "oppositeDirection" : true, "depth" : 20 * mm});
        }
        {
            var Q0;
            Q0=makeQuery(id+"F36.opExtrude","SWEPT_BODY",BODY,{"disambiguationData":[OSD([sQuery(id+"F35.wireOp",EDGE,"E188.bottom"),sQuery(id+"F35.wireOp",EDGE,"E188.top"),sQuery(id+"F35.wireOp",EDGE,"E188.left"),sQuery(id+"F35.wireOp",EDGE,"E188.right"),sQuery(id+"F35.wireOp",EDGE,"E191"),sQuery(id+"F35.wireOp",EDGE,"E192"),sQuery(id+"F35.wireOp",EDGE,"E193"),sQuery(id+"F35.wireOp",EDGE,"E194"),sQuery(id+"F35.wireOp",EDGE,"E195"),sQuery(id+"F35.wireOp",EDGE,"E203.trimOffspring"),sQuery(id+"F35.wireOp",EDGE,"E205.trimOffspring"),sQuery(id+"F35.wireOp",EDGE,"E207.trimOffspring"),sQuery(id+"F35.wireOp",EDGE,"E208.trimOffspring"),sQuery(id+"F35.wireOp",EDGE,"E209.trimOffspring"),sQuery(id+"F35.wireOp",EDGE,"E210.trimOffspring"),sQuery(id+"F35.wireOp",EDGE,"E213.trimOffspring"),sQuery(id+"F35.wireOp",EDGE,"E214"),sQuery(id+"F35.wireOp",EDGE,"E215"),sQuery(id+"F35.wireOp",EDGE,"E216"),sQuery(id+"F35.wireOp",EDGE,"E217"),sQuery(id+"F35.wireOp",EDGE,"E218"),sQuery(id+"F35.wireOp",EDGE,"E219"),sQuery(id+"F35.wireOp",EDGE,"E220"),sQuery(id+"F35.wireOp",EDGE,"E221"),sQuery(id+"F35.wireOp",EDGE,"E222"),sQuery(id+"F35.wireOp",EDGE,"E223.bottom"),sQuery(id+"F35.wireOp",EDGE,"E223.top"),sQuery(id+"F35.wireOp",EDGE,"E223.left"),sQuery(id+"F35.wireOp",EDGE,"E223.right"),sQuery(id+"F35.wireOp",EDGE,"E224.bottom"),sQuery(id+"F35.wireOp",EDGE,"E196.bottom"),sQuery(id+"F35.wireOp",EDGE,"E224.left"),sQuery(id+"F35.wireOp",EDGE,"E225.trimOffspring"),sQuery(id+"F35.wireOp",EDGE,"E226.trimOffspring"),sQuery(id+"F35.wireOp",EDGE,"E227.trimOffspring"),sQuery(id+"F35.wireOp",EDGE,"E228.trimOffspring"),sQuery(id+"F35.wireOp",EDGE,"E229.trimOffspring"),sQuery(id+"F35.wireOp",EDGE,"E230.trimOffspring"),sQuery(id+"F35.wireOp",EDGE,"E231.trimOffspring"),sQuery(id+"F35.wireOp",EDGE,"E233.trimOffspring"),sQuery(id+"F35.wireOp",EDGE,"E232.trimOffspring"),sQuery(id+"F35.wireOp",EDGE,"E234.trimOffspring"),sQuery(id+"F35.wireOp",EDGE,"E235.trimOffspring"),sQuery(id+"F35.wireOp",EDGE,"E236.trimOffspring"),sQuery(id+"F35.wireOp",EDGE,"E237.filletArc"),sQuery(id+"F35.wireOp",EDGE,"E238.filletArc"),sQuery(id+"F35.wireOp",EDGE,"E239.filletArc"),sQuery(id+"F35.wireOp",EDGE,"E240.filletArc"),sQuery(id+"F35.wireOp",EDGE,"E241")])]});
            var Q1;
            Q1=qCreatedBy(id+"F10.planeOp",FACE);
            mirror(context, id + "F39", {"entities" : qUnion([Q0]), "mirrorPlane" : qUnion([Q1])});
        }
        {
            var Q0;
            Q0=makeQuery(id+"F36.opExtrude","SWEPT_BODY",BODY,{"disambiguationData":[OSD([sQuery(id+"F35.wireOp",EDGE,"E188.bottom"),sQuery(id+"F35.wireOp",EDGE,"E188.top"),sQuery(id+"F35.wireOp",EDGE,"E188.left"),sQuery(id+"F35.wireOp",EDGE,"E188.right"),sQuery(id+"F35.wireOp",EDGE,"E191"),sQuery(id+"F35.wireOp",EDGE,"E192"),sQuery(id+"F35.wireOp",EDGE,"E193"),sQuery(id+"F35.wireOp",EDGE,"E194"),sQuery(id+"F35.wireOp",EDGE,"E195"),sQuery(id+"F35.wireOp",EDGE,"E203.trimOffspring"),sQuery(id+"F35.wireOp",EDGE,"E205.trimOffspring"),sQuery(id+"F35.wireOp",EDGE,"E207.trimOffspring"),sQuery(id+"F35.wireOp",EDGE,"E208.trimOffspring"),sQuery(id+"F35.wireOp",EDGE,"E209.trimOffspring"),sQuery(id+"F35.wireOp",EDGE,"E210.trimOffspring"),sQuery(id+"F35.wireOp",EDGE,"E213.trimOffspring"),sQuery(id+"F35.wireOp",EDGE,"E214"),sQuery(id+"F35.wireOp",EDGE,"E215"),sQuery(id+"F35.wireOp",EDGE,"E216"),sQuery(id+"F35.wireOp",EDGE,"E217"),sQuery(id+"F35.wireOp",EDGE,"E218"),sQuery(id+"F35.wireOp",EDGE,"E219"),sQuery(id+"F35.wireOp",EDGE,"E220"),sQuery(id+"F35.wireOp",EDGE,"E221"),sQuery(id+"F35.wireOp",EDGE,"E222"),sQuery(id+"F35.wireOp",EDGE,"E223.bottom"),sQuery(id+"F35.wireOp",EDGE,"E223.top"),sQuery(id+"F35.wireOp",EDGE,"E223.left"),sQuery(id+"F35.wireOp",EDGE,"E223.right"),sQuery(id+"F35.wireOp",EDGE,"E224.bottom"),sQuery(id+"F35.wireOp",EDGE,"E196.bottom"),sQuery(id+"F35.wireOp",EDGE,"E224.left"),sQuery(id+"F35.wireOp",EDGE,"E225.trimOffspring"),sQuery(id+"F35.wireOp",EDGE,"E226.trimOffspring"),sQuery(id+"F35.wireOp",EDGE,"E227.trimOffspring"),sQuery(id+"F35.wireOp",EDGE,"E228.trimOffspring"),sQuery(id+"F35.wireOp",EDGE,"E229.trimOffspring"),sQuery(id+"F35.wireOp",EDGE,"E230.trimOffspring"),sQuery(id+"F35.wireOp",EDGE,"E231.trimOffspring"),sQuery(id+"F35.wireOp",EDGE,"E233.trimOffspring"),sQuery(id+"F35.wireOp",EDGE,"E232.trimOffspring"),sQuery(id+"F35.wireOp",EDGE,"E234.trimOffspring"),sQuery(id+"F35.wireOp",EDGE,"E235.trimOffspring"),sQuery(id+"F35.wireOp",EDGE,"E236.trimOffspring"),sQuery(id+"F35.wireOp",EDGE,"E237.filletArc"),sQuery(id+"F35.wireOp",EDGE,"E238.filletArc"),sQuery(id+"F35.wireOp",EDGE,"E239.filletArc"),sQuery(id+"F35.wireOp",EDGE,"E240.filletArc"),sQuery(id+"F35.wireOp",EDGE,"E241")])]});
            var Q1;
            Q1=qCreatedBy(id+"F9.planeOp",FACE);
            mirror(context, id + "F40", {"entities" : qUnion([Q0]), "mirrorPlane" : qUnion([Q1])});
        }
        {
            var Q0;
            Q0=makeQuery(id+"F39.opPattern","COPY",BODY,{"derivedFrom":makeQuery(id+"F36.opExtrude","SWEPT_BODY",BODY,{"disambiguationData":[OSD([sQuery(id+"F35.wireOp",EDGE,"E188.bottom"),sQuery(id+"F35.wireOp",EDGE,"E188.top"),sQuery(id+"F35.wireOp",EDGE,"E188.left"),sQuery(id+"F35.wireOp",EDGE,"E188.right"),sQuery(id+"F35.wireOp",EDGE,"E191"),sQuery(id+"F35.wireOp",EDGE,"E192"),sQuery(id+"F35.wireOp",EDGE,"E193"),sQuery(id+"F35.wireOp",EDGE,"E194"),sQuery(id+"F35.wireOp",EDGE,"E195"),sQuery(id+"F35.wireOp",EDGE,"E203.trimOffspring"),sQuery(id+"F35.wireOp",EDGE,"E205.trimOffspring"),sQuery(id+"F35.wireOp",EDGE,"E207.trimOffspring"),sQuery(id+"F35.wireOp",EDGE,"E208.trimOffspring"),sQuery(id+"F35.wireOp",EDGE,"E209.trimOffspring"),sQuery(id+"F35.wireOp",EDGE,"E210.trimOffspring"),sQuery(id+"F35.wireOp",EDGE,"E213.trimOffspring"),sQuery(id+"F35.wireOp",EDGE,"E214"),sQuery(id+"F35.wireOp",EDGE,"E215"),sQuery(id+"F35.wireOp",EDGE,"E216"),sQuery(id+"F35.wireOp",EDGE,"E217"),sQuery(id+"F35.wireOp",EDGE,"E218"),sQuery(id+"F35.wireOp",EDGE,"E219"),sQuery(id+"F35.wireOp",EDGE,"E220"),sQuery(id+"F35.wireOp",EDGE,"E221"),sQuery(id+"F35.wireOp",EDGE,"E222"),sQuery(id+"F35.wireOp",EDGE,"E223.bottom"),sQuery(id+"F35.wireOp",EDGE,"E223.top"),sQuery(id+"F35.wireOp",EDGE,"E223.left"),sQuery(id+"F35.wireOp",EDGE,"E223.right"),sQuery(id+"F35.wireOp",EDGE,"E224.bottom"),sQuery(id+"F35.wireOp",EDGE,"E196.bottom"),sQuery(id+"F35.wireOp",EDGE,"E224.left"),sQuery(id+"F35.wireOp",EDGE,"E225.trimOffspring"),sQuery(id+"F35.wireOp",EDGE,"E226.trimOffspring"),sQuery(id+"F35.wireOp",EDGE,"E227.trimOffspring"),sQuery(id+"F35.wireOp",EDGE,"E228.trimOffspring"),sQuery(id+"F35.wireOp",EDGE,"E229.trimOffspring"),sQuery(id+"F35.wireOp",EDGE,"E230.trimOffspring"),sQuery(id+"F35.wireOp",EDGE,"E231.trimOffspring"),sQuery(id+"F35.wireOp",EDGE,"E233.trimOffspring"),sQuery(id+"F35.wireOp",EDGE,"E232.trimOffspring"),sQuery(id+"F35.wireOp",EDGE,"E234.trimOffspring"),sQuery(id+"F35.wireOp",EDGE,"E235.trimOffspring"),sQuery(id+"F35.wireOp",EDGE,"E236.trimOffspring"),sQuery(id+"F35.wireOp",EDGE,"E237.filletArc"),sQuery(id+"F35.wireOp",EDGE,"E238.filletArc"),sQuery(id+"F35.wireOp",EDGE,"E239.filletArc"),sQuery(id+"F35.wireOp",EDGE,"E240.filletArc"),sQuery(id+"F35.wireOp",EDGE,"E241")])]}),"instanceName":"1"});
            var Q1;
            Q1=qCreatedBy(id+"F9.planeOp",FACE);
            mirror(context, id + "F41", {"entities" : qUnion([Q0]), "mirrorPlane" : qUnion([Q1])});
        }
        {
            var Q0;
            Q0=makeQuery(id+"F36.opExtrude","SWEPT_FACE",FACE,{"disambiguationData":[OSD([sQuery(id+"F35.wireOp",EDGE,"E231.trimOffspring")])]});
            var sketch = newSketch(context, id + "F42", { "sketchPlane" : qUnion([Q0])});
            skLineSegment(sketch, "E252.left", {"start": v(-14, 331) * mm, "end": v(-14, 314) * mm});
            skLineSegment(sketch, "E252.right", {"start": v(-34, 331) * mm, "end": v(-34, 314) * mm});
            skLineSegment(sketch, "E253.bottom", {"start": v(-26.85, 325.75) * mm, "end": v(-24.35, 325.75) * mm});
            skLineSegment(sketch, "E253.top", {"start": v(-27.05, 319.25) * mm, "end": v(-24.35, 319.25) * mm});
            skLineSegment(sketch, "E254", {"start": v(-34, 322.5) * mm, "end": v(-14, 322.5) * mm, "construction": true});
            skPoint(sketch, "E255.first.point", {"position": v(-28.3, 325.75) * mm});
            skPoint(sketch, "E255.second.point", {"position": v(-27.05, 319.25) * mm});
            skPoint(sketch, "E255.third.point", {"position": v(-30.1, 322.5) * mm});
            skArc(sketch, "E256", {"start": v(-26.85, 325.75) * mm, "mid": v(-30.1, 322.5) * mm, "end": v(-26.85, 319.25) * mm});
            skArc(sketch, "E257", {"start": v(-24.35, 319.25) * mm, "mid": v(-21.1, 322.5) * mm, "end": v(-24.35, 325.75) * mm});
            skPoint(sketch, "E258.orphan", {"position": v(-30.1, 325.75) * mm});
            skPoint(sketch, "E253.left.end.orphan", {"position": v(-30.1, 319.25) * mm});
            skLineSegment(sketch, "E259.bottom", {"start": v(-34, 331) * mm, "end": v(-14, 331) * mm});
            skLineSegment(sketch, "E259.top", {"start": v(-34, 314) * mm, "end": v(-14, 314) * mm});
            skPoint(sketch, "E260.orphan", {"position": v(-34, 332.5) * mm});
            skPoint(sketch, "E261.orphan", {"position": v(-14, 415) * mm});
            skPoint(sketch, "E252.top.start.orphan", {"position": v(-14, 230) * mm});
            skPoint(sketch, "E262.orphan", {"position": v(-34, 312.5) * mm});
            skSolve(sketch);
        }
        {
            var Q0;
            Q0 = qSketchRegion(id + "F42", true);
            extrude(context, id + "F43", {"entities" : qUnion([Q0]), "depth" : 3.2 * mm});
        }
        {
            var Q0;
            Q0=makeQuery(id+"F43.opExtrude","CAP_FACE",FACE,{"disambiguationData":[OSD([sQuery(id+"F42.wireOp",EDGE,"E253.bottom"),sQuery(id+"F42.wireOp",EDGE,"E253.top"),sQuery(id+"F42.wireOp",EDGE,"E256"),sQuery(id+"F42.wireOp",EDGE,"E257"),sQuery(id+"F42.wireOp",EDGE,"E259.bottom"),sQuery(id+"F42.wireOp",EDGE,"E259.top"),sQuery(id+"F42.wireOp",EDGE,"E252.right"),sQuery(id+"F42.wireOp",EDGE,"E252.left")])],"isStart":false});
            var sketch = newSketch(context, id + "F44", { "sketchPlane" : qUnion([Q0])});
            skLineSegment(sketch, "E263.bottom", {"start": v(-14, 331) * mm, "end": v(-17.2, 331) * mm});
            skLineSegment(sketch, "E263.top", {"start": v(-14, 314) * mm, "end": v(-17.2, 314) * mm});
            skLineSegment(sketch, "E263.left", {"start": v(-14, 331) * mm, "end": v(-14, 314) * mm});
            skLineSegment(sketch, "E263.right", {"start": v(-17.2, 331) * mm, "end": v(-17.2, 314) * mm});
            skSolve(sketch);
        }
        {
            var Q0;
            Q0 = qSketchRegion(id + "F44", true);
            extrude(context, id + "F45", {"entities" : qUnion([Q0]), "depth" : (20 - 3.2) * mm});
        }
        {
            var Q0;
            Q0=makeQuery(id+"F43.opExtrude","SWEPT_BODY",BODY,{"disambiguationData":[OSD([sQuery(id+"F42.wireOp",EDGE,"E253.bottom"),sQuery(id+"F42.wireOp",EDGE,"E253.top"),sQuery(id+"F42.wireOp",EDGE,"E256"),sQuery(id+"F42.wireOp",EDGE,"E257"),sQuery(id+"F42.wireOp",EDGE,"E259.bottom"),sQuery(id+"F42.wireOp",EDGE,"E259.top"),sQuery(id+"F42.wireOp",EDGE,"E252.right"),sQuery(id+"F42.wireOp",EDGE,"E252.left")])]});
            var Q1;
            Q1=makeQuery(id+"F45.opExtrude","SWEPT_BODY",BODY,{"disambiguationData":[OSD([sQuery(id+"F44.wireOp",EDGE,"E263.bottom"),sQuery(id+"F44.wireOp",EDGE,"E263.top"),sQuery(id+"F44.wireOp",EDGE,"E263.left"),sQuery(id+"F44.wireOp",EDGE,"E263.right")])]});
            booleanBodies(context, id + "F46", {"operationType" : BooleanOperationType.UNION, "tools" : qUnion([Q0, Q1])});
        }
        {
            var Q0;
            Q0=makeQuery(id+"F45.opExtrude","SWEPT_FACE",FACE,{"disambiguationData":[OSD([sQuery(id+"F44.wireOp",EDGE,"E263.right")])]});
            var sketch = newSketch(context, id + "F47", { "sketchPlane" : qUnion([Q0])});
            skLineSegment(sketch, "E264.bottom", {"start": v(33.35, 319.25) * mm, "end": v(35.85, 319.25) * mm});
            skLineSegment(sketch, "E264.top", {"start": v(33.35, 325.75) * mm, "end": v(35.85, 325.75) * mm});
            skLineSegment(sketch, "E265", {"start": v(26.2, 322.5) * mm, "end": v(43, 322.5) * mm, "construction": true});
            skArc(sketch, "E266", {"start": v(33.35, 325.75) * mm, "mid": v(30.1, 322.5) * mm, "end": v(33.35, 319.25) * mm});
            skArc(sketch, "E267", {"start": v(35.85, 319.25) * mm, "mid": v(39.1, 322.5) * mm, "end": v(35.85, 325.75) * mm});
            skSolve(sketch);
        }
        {
            var Q0;
            Q0 = qSketchRegion(id + "F47", true);
            extrude(context, id + "F48", {"entities" : qUnion([Q0]), "operationType" : NewBodyOperationType.REMOVE, "endBound" : BoundingType.THROUGH_ALL, "oppositeDirection" : true, "depth" : 25 * mm});
        }
        {
            var Q0;
            Q0=makeQuery(id+"F46.opBoolean","MERGE",FACE,{"derivedFrom":[makeQuery(id+"F43.opExtrude","SWEPT_FACE",FACE,{"disambiguationData":[OSD([sQuery(id+"F42.wireOp",EDGE,"E259.bottom")])]}),makeQuery(id+"F45.opExtrude","SWEPT_FACE",FACE,{"disambiguationData":[OSD([sQuery(id+"F44.wireOp",EDGE,"E263.bottom")])]})]});
            var sketch = newSketch(context, id + "F49", { "sketchPlane" : qUnion([Q0])});
            skLineSegment(sketch, "E268", {"start": v(34, 26.2) * mm, "end": v(17.2, 43) * mm});
            skLineSegment(sketch, "E269", {"start": v(17.2, 43) * mm, "end": v(17.2, 26.2) * mm});
            skLineSegment(sketch, "E270", {"start": v(17.2, 26.2) * mm, "end": v(34, 26.2) * mm});
            skSolve(sketch);
        }
        {
            var Q0;
            Q0 = qSketchRegion(id + "F49", true);
            extrude(context, id + "F50", {"entities" : qUnion([Q0]), "operationType" : NewBodyOperationType.ADD, "oppositeDirection" : true, "depth" : 2.1 * mm});
        }
        {
            var Q0;
            Q0=makeQuery(id+"F46.opBoolean","MERGE",FACE,{"derivedFrom":[makeQuery(id+"F43.opExtrude","SWEPT_FACE",FACE,{"disambiguationData":[OSD([sQuery(id+"F42.wireOp",EDGE,"E259.top")])]}),makeQuery(id+"F45.opExtrude","SWEPT_FACE",FACE,{"disambiguationData":[OSD([sQuery(id+"F44.wireOp",EDGE,"E263.top")])]})]});
            var sketch = newSketch(context, id + "F51", { "sketchPlane" : qUnion([Q0])});
            skLineSegment(sketch, "E271", {"start": v(34, -26.2) * mm, "end": v(17.2, -43) * mm});
            skLineSegment(sketch, "E272", {"start": v(17.2, -43) * mm, "end": v(17.2, -26.2) * mm});
            skLineSegment(sketch, "E273", {"start": v(17.2, -26.2) * mm, "end": v(34, -26.2) * mm});
            skSolve(sketch);
        }
        {
            var Q0;
            Q0 = qSketchRegion(id + "F51", true);
            extrude(context, id + "F52", {"entities" : qUnion([Q0]), "operationType" : NewBodyOperationType.ADD, "oppositeDirection" : true, "depth" : 2.1 * mm});
        }
        {
            var Q0;
            Q0=makeQuery(id+"F43.opExtrude","SWEPT_BODY",BODY,{"disambiguationData":[OSD([sQuery(id+"F42.wireOp",EDGE,"E253.bottom"),sQuery(id+"F42.wireOp",EDGE,"E253.top"),sQuery(id+"F42.wireOp",EDGE,"E256"),sQuery(id+"F42.wireOp",EDGE,"E257"),sQuery(id+"F42.wireOp",EDGE,"E259.bottom"),sQuery(id+"F42.wireOp",EDGE,"E259.top"),sQuery(id+"F42.wireOp",EDGE,"E252.right"),sQuery(id+"F42.wireOp",EDGE,"E252.left")])]});
            var Q1;
            Q1=qCreatedBy(id+"F8.planeOp",FACE);
            mirror(context, id + "F53", {"entities" : qUnion([Q0]), "mirrorPlane" : qUnion([Q1])});
        }
        {
            var Q0;
            Q0=makeQuery(id+"F43.opExtrude","SWEPT_BODY",BODY,{"disambiguationData":[OSD([sQuery(id+"F42.wireOp",EDGE,"E253.bottom"),sQuery(id+"F42.wireOp",EDGE,"E253.top"),sQuery(id+"F42.wireOp",EDGE,"E256"),sQuery(id+"F42.wireOp",EDGE,"E257"),sQuery(id+"F42.wireOp",EDGE,"E259.bottom"),sQuery(id+"F42.wireOp",EDGE,"E259.top"),sQuery(id+"F42.wireOp",EDGE,"E252.right"),sQuery(id+"F42.wireOp",EDGE,"E252.left")])]});
            var Q1;
            Q1=qCreatedBy(id+"F10.planeOp",FACE);
            mirror(context, id + "F54", {"entities" : qUnion([Q0]), "mirrorPlane" : qUnion([Q1])});
        }
        {
            var Q0;
            Q0=makeQuery(id+"F53.opPattern","COPY",BODY,{"derivedFrom":makeQuery(id+"F43.opExtrude","SWEPT_BODY",BODY,{"disambiguationData":[OSD([sQuery(id+"F42.wireOp",EDGE,"E253.bottom"),sQuery(id+"F42.wireOp",EDGE,"E253.top"),sQuery(id+"F42.wireOp",EDGE,"E256"),sQuery(id+"F42.wireOp",EDGE,"E257"),sQuery(id+"F42.wireOp",EDGE,"E259.bottom"),sQuery(id+"F42.wireOp",EDGE,"E259.top"),sQuery(id+"F42.wireOp",EDGE,"E252.right"),sQuery(id+"F42.wireOp",EDGE,"E252.left")])]}),"instanceName":"1"});
            var Q1;
            Q1=qCreatedBy(id+"F10.planeOp",FACE);
            mirror(context, id + "F55", {"entities" : qUnion([Q0]), "mirrorPlane" : qUnion([Q1])});
        }
        {
            var Q0;
            Q0=makeQuery(id+"F43.opExtrude","SWEPT_BODY",BODY,{"disambiguationData":[OSD([sQuery(id+"F42.wireOp",EDGE,"E253.bottom"),sQuery(id+"F42.wireOp",EDGE,"E253.top"),sQuery(id+"F42.wireOp",EDGE,"E256"),sQuery(id+"F42.wireOp",EDGE,"E257"),sQuery(id+"F42.wireOp",EDGE,"E259.bottom"),sQuery(id+"F42.wireOp",EDGE,"E259.top"),sQuery(id+"F42.wireOp",EDGE,"E252.right"),sQuery(id+"F42.wireOp",EDGE,"E252.left")])]});
            var Q1;
            Q1=qCreatedBy(id+"F9.planeOp",FACE);
            mirror(context, id + "F56", {"entities" : qUnion([Q0]), "mirrorPlane" : qUnion([Q1])});
        }
        {
            var Q0;
            Q0=makeQuery(id+"F53.opPattern","COPY",BODY,{"derivedFrom":makeQuery(id+"F43.opExtrude","SWEPT_BODY",BODY,{"disambiguationData":[OSD([sQuery(id+"F42.wireOp",EDGE,"E253.bottom"),sQuery(id+"F42.wireOp",EDGE,"E253.top"),sQuery(id+"F42.wireOp",EDGE,"E256"),sQuery(id+"F42.wireOp",EDGE,"E257"),sQuery(id+"F42.wireOp",EDGE,"E259.bottom"),sQuery(id+"F42.wireOp",EDGE,"E259.top"),sQuery(id+"F42.wireOp",EDGE,"E252.right"),sQuery(id+"F42.wireOp",EDGE,"E252.left")])]}),"instanceName":"1"});
            var Q1;
            Q1=qCreatedBy(id+"F9.planeOp",FACE);
            mirror(context, id + "F57", {"entities" : qUnion([Q0]), "mirrorPlane" : qUnion([Q1])});
        }
        {
            var Q0;
            Q0=makeQuery(id+"F54.opPattern","COPY",BODY,{"derivedFrom":makeQuery(id+"F43.opExtrude","SWEPT_BODY",BODY,{"disambiguationData":[OSD([sQuery(id+"F42.wireOp",EDGE,"E253.bottom"),sQuery(id+"F42.wireOp",EDGE,"E253.top"),sQuery(id+"F42.wireOp",EDGE,"E256"),sQuery(id+"F42.wireOp",EDGE,"E257"),sQuery(id+"F42.wireOp",EDGE,"E259.bottom"),sQuery(id+"F42.wireOp",EDGE,"E259.top"),sQuery(id+"F42.wireOp",EDGE,"E252.right"),sQuery(id+"F42.wireOp",EDGE,"E252.left")])]}),"instanceName":"1"});
            var Q1;
            Q1=qCreatedBy(id+"F9.planeOp",FACE);
            mirror(context, id + "F58", {"entities" : qUnion([Q0]), "mirrorPlane" : qUnion([Q1])});
        }
        {
            var Q0;
            Q0=makeQuery(id+"F55.opPattern","COPY",BODY,{"derivedFrom":makeQuery(id+"F53.opPattern","COPY",BODY,{"derivedFrom":makeQuery(id+"F43.opExtrude","SWEPT_BODY",BODY,{"disambiguationData":[OSD([sQuery(id+"F42.wireOp",EDGE,"E253.bottom"),sQuery(id+"F42.wireOp",EDGE,"E253.top"),sQuery(id+"F42.wireOp",EDGE,"E256"),sQuery(id+"F42.wireOp",EDGE,"E257"),sQuery(id+"F42.wireOp",EDGE,"E259.bottom"),sQuery(id+"F42.wireOp",EDGE,"E259.top"),sQuery(id+"F42.wireOp",EDGE,"E252.right"),sQuery(id+"F42.wireOp",EDGE,"E252.left")])]}),"instanceName":"1"}),"instanceName":"1"});
            var Q1;
            Q1=qCreatedBy(id+"F9.planeOp",FACE);
            mirror(context, id + "F59", {"entities" : qUnion([Q0]), "mirrorPlane" : qUnion([Q1])});
        }
        {
            var Q0;
            Q0=makeQuery(id+"F22.opPattern","COPY",FACE,{"derivedFrom":makeQuery(id+"F21.opExtrude","CAP_FACE",FACE,{"disambiguationData":[OSD([sQuery(id+"F20.wireOp",EDGE,"E141.bottom"),sQuery(id+"F20.wireOp",EDGE,"E141.top"),sQuery(id+"F20.wireOp",EDGE,"E141.left"),sQuery(id+"F20.wireOp",EDGE,"E141.right"),sQuery(id+"F20.wireOp",EDGE,"E142.filletArc"),sQuery(id+"F20.wireOp",EDGE,"E143.filletArc"),sQuery(id+"F20.wireOp",EDGE,"E144.filletArc"),sQuery(id+"F20.wireOp",EDGE,"E145.filletArc"),sQuery(id+"F20.wireOp",EDGE,"E148"),sQuery(id+"F20.wireOp",EDGE,"E149"),sQuery(id+"F20.wireOp",EDGE,"E150"),sQuery(id+"F20.wireOp",EDGE,"E151"),sQuery(id+"F20.wireOp",EDGE,"E152"),sQuery(id+"F20.wireOp",EDGE,"E153"),sQuery(id+"F20.wireOp",EDGE,"E154"),sQuery(id+"F20.wireOp",EDGE,"E155"),sQuery(id+"F20.wireOp",EDGE,"E156"),sQuery(id+"F20.wireOp",EDGE,"E157"),sQuery(id+"F20.wireOp",EDGE,"E158"),sQuery(id+"F20.wireOp",EDGE,"E159"),sQuery(id+"F20.wireOp",EDGE,"E160"),sQuery(id+"F20.wireOp",EDGE,"E161"),sQuery(id+"F20.wireOp",EDGE,"E162"),sQuery(id+"F20.wireOp",EDGE,"E163"),sQuery(id+"F20.wireOp",EDGE,"E164"),sQuery(id+"F20.wireOp",EDGE,"E165"),sQuery(id+"F20.wireOp",EDGE,"E172"),sQuery(id+"F20.wireOp",EDGE,"E173")])],"isStart":false}),"instanceName":"1"});
            var sketch = newSketch(context, id + "F60", { "sketchPlane" : qUnion([Q0])});
            skLineSegment(sketch, "E274.bottom", {"start": v(32, -31) * mm, "end": v(150, -31) * mm});
            skLineSegment(sketch, "E274.top", {"start": v(32, -387) * mm, "end": v(150, -387) * mm});
            skLineSegment(sketch, "E274.right", {"start": v(160, -41) * mm, "end": v(160, -98.75) * mm});
            skLineSegment(sketch, "E275", {"start": v(22, -191.5) * mm, "end": v(22, -133.75) * mm});
            skLineSegment(sketch, "E276", {"start": v(160, -226.5) * mm, "end": v(160, -284.25) * mm});
            skLineSegment(sketch, "E277", {"start": v(32, -108.75) * mm, "end": v(150, -108.75) * mm});
            skLineSegment(sketch, "E278", {"start": v(150, -123.75) * mm, "end": v(32, -123.75) * mm});
            skLineSegment(sketch, "E279", {"start": v(32, -201.5) * mm, "end": v(150, -201.5) * mm});
            skLineSegment(sketch, "E280", {"start": v(150, -216.5) * mm, "end": v(32, -216.5) * mm});
            skLineSegment(sketch, "E281", {"start": v(32, -294.25) * mm, "end": v(150, -294.25) * mm});
            skLineSegment(sketch, "E282", {"start": v(150, -309.25) * mm, "end": v(32, -309.25) * mm});
            skLineSegment(sketch, "E283.trimOffspring", {"start": v(22, -98.75) * mm, "end": v(22, -41) * mm});
            skLineSegment(sketch, "E284.trimOffspring", {"start": v(160, -133.75) * mm, "end": v(160, -191.5) * mm});
            skLineSegment(sketch, "E285.trimOffspring", {"start": v(160, -319.25) * mm, "end": v(160, -377) * mm});
            skLineSegment(sketch, "E286.trimOffspring", {"start": v(22, -319.25) * mm, "end": v(22, -377) * mm});
            skLineSegment(sketch, "E287", {"start": v(22, -226.5) * mm, "end": v(22, -284.25) * mm});
            skPoint(sketch, "E288.visualSharp", {"position": v(22, -108.75) * mm});
            skArc(sketch, "E288.filletArc", {"start": v(22, -98.75) * mm, "mid": v(24.93, -105.82) * mm, "end": v(32, -108.75) * mm});
            skPoint(sketch, "E289.visualSharp", {"position": v(22, -31) * mm});
            skArc(sketch, "E289.filletArc", {"start": v(32, -31) * mm, "mid": v(24.93, -33.93) * mm, "end": v(22, -41) * mm});
            skPoint(sketch, "E290.visualSharp", {"position": v(160, -31) * mm});
            skArc(sketch, "E290.filletArc", {"start": v(160, -41) * mm, "mid": v(157.07, -33.93) * mm, "end": v(150, -31) * mm});
            skPoint(sketch, "E291.visualSharp", {"position": v(160, -108.75) * mm});
            skArc(sketch, "E291.filletArc", {"start": v(150, -108.75) * mm, "mid": v(157.07, -105.82) * mm, "end": v(160, -98.75) * mm});
            skPoint(sketch, "E292.visualSharp", {"position": v(22, -201.5) * mm});
            skArc(sketch, "E292.filletArc", {"start": v(22, -191.5) * mm, "mid": v(24.93, -198.57) * mm, "end": v(32, -201.5) * mm});
            skPoint(sketch, "E293.visualSharp", {"position": v(22, -216.5) * mm});
            skArc(sketch, "E293.filletArc", {"start": v(32, -216.5) * mm, "mid": v(24.93, -219.43) * mm, "end": v(22, -226.5) * mm});
            skPoint(sketch, "E294.visualSharp", {"position": v(160, -201.5) * mm});
            skArc(sketch, "E294.filletArc", {"start": v(150, -201.5) * mm, "mid": v(157.07, -198.57) * mm, "end": v(160, -191.5) * mm});
            skPoint(sketch, "E295.visualSharp", {"position": v(160, -216.5) * mm});
            skArc(sketch, "E295.filletArc", {"start": v(160, -226.5) * mm, "mid": v(157.07, -219.43) * mm, "end": v(150, -216.5) * mm});
            skArc(sketch, "E296.filletArc", {"start": v(150, -294.25) * mm, "mid": v(157.07, -291.32) * mm, "end": v(160, -284.25) * mm});
            skArc(sketch, "E297.filletArc", {"start": v(160, -319.25) * mm, "mid": v(157.07, -312.18) * mm, "end": v(150, -309.25) * mm});
            skPoint(sketch, "E298.visualSharp", {"position": v(160, -387) * mm});
            skArc(sketch, "E298.filletArc", {"start": v(150, -387) * mm, "mid": v(157.07, -384.07) * mm, "end": v(160, -377) * mm});
            skPoint(sketch, "E299.visualSharp", {"position": v(22, -309.25) * mm});
            skArc(sketch, "E299.filletArc", {"start": v(32, -309.25) * mm, "mid": v(24.93, -312.18) * mm, "end": v(22, -319.25) * mm});
            skPoint(sketch, "E300.visualSharp", {"position": v(22, -387) * mm});
            skArc(sketch, "E300.filletArc", {"start": v(22, -377) * mm, "mid": v(24.93, -384.07) * mm, "end": v(32, -387) * mm});
            skPoint(sketch, "E301.visualSharp", {"position": v(22, -294.25) * mm});
            skArc(sketch, "E301.filletArc", {"start": v(22, -284.25) * mm, "mid": v(24.93, -291.32) * mm, "end": v(32, -294.25) * mm});
            skPoint(sketch, "E302.visualSharp", {"position": v(22, -123.75) * mm});
            skArc(sketch, "E302.filletArc", {"start": v(32, -123.75) * mm, "mid": v(24.93, -126.68) * mm, "end": v(22, -133.75) * mm});
            skPoint(sketch, "E303.visualSharp", {"position": v(160, -123.75) * mm});
            skArc(sketch, "E303.filletArc", {"start": v(160, -133.75) * mm, "mid": v(157.07, -126.68) * mm, "end": v(150, -123.75) * mm});
            skSolve(sketch);
        }
        {
            var Q0;
            Q0 = qSketchRegion(id + "F60", true);
            extrude(context, id + "F61", {"entities" : qUnion([Q0]), "operationType" : NewBodyOperationType.REMOVE, "oppositeDirection" : true, "depth" : 3 * mm});
        }
        {
            var Q0;
            Q0=makeQuery(id+"F19.opPattern","COPY",FACE,{"derivedFrom":makeQuery(id+"F1.opExtrude","CAP_FACE",FACE,{"disambiguationData":[OSD([sQuery(id+"F0.wireOp",EDGE,"E0.bottom"),sQuery(id+"F0.wireOp",EDGE,"E0.top"),sQuery(id+"F0.wireOp",EDGE,"E0.left"),sQuery(id+"F0.wireOp",EDGE,"E0.right")])],"isStart":false}),"instanceName":"1"});
            var sketch = newSketch(context, id + "F62", { "sketchPlane" : qUnion([Q0])});
            skLineSegment(sketch, "E304.bottom", {"start": v(74.5, 114) * mm, "end": v(172, 114) * mm});
            skLineSegment(sketch, "E304.top", {"start": v(74.5, 312.5) * mm, "end": v(172, 312.5) * mm});
            skLineSegment(sketch, "E304.left", {"start": v(74.5, 114) * mm, "end": v(74.5, 312.5) * mm});
            skLineSegment(sketch, "E304.right", {"start": v(172, 114) * mm, "end": v(172, 312.5) * mm});
            skSolve(sketch);
        }
        {
            var Q0;
            Q0 = qSketchRegion(id + "F62", true);
            extrude(context, id + "F63", {"entities" : qUnion([Q0]), "depth" : 43.5 * mm});
        }
        {
            var Q0;
            Q0=makeQuery(id+"F1.opExtrude","CAP_FACE",FACE,{"disambiguationData":[OSD([sQuery(id+"F0.wireOp",EDGE,"E0.bottom"),sQuery(id+"F0.wireOp",EDGE,"E0.top"),sQuery(id+"F0.wireOp",EDGE,"E0.left"),sQuery(id+"F0.wireOp",EDGE,"E0.right")])],"isStart":false});
            var sketch = newSketch(context, id + "F64", { "sketchPlane" : qUnion([Q0])});
            skLineSegment(sketch, "E305.bottom", {"start": v(-165.25, 101.5) * mm, "end": v(-16.75, 101.5) * mm});
            skLineSegment(sketch, "E305.top", {"start": v(-165.25, 20) * mm, "end": v(-16.75, 20) * mm});
            skLineSegment(sketch, "E305.left", {"start": v(-165.25, 101.5) * mm, "end": v(-165.25, 20) * mm});
            skLineSegment(sketch, "E305.right", {"start": v(-16.75, 101.5) * mm, "end": v(-16.75, 20) * mm});
            skLineSegment(sketch, "E306.0", {"start": v(-168, 312.5) * mm, "end": v(-14, 312.5) * mm, "construction": true});
            skLineSegment(sketch, "E307", {"start": v(-91, 312.5) * mm, "end": v(-91, 221.05) * mm, "construction": true});
            skLineSegment(sketch, "E308", {"start": v(-91, 101.5) * mm, "end": v(-91, 152.72) * mm, "construction": true});
            skSolve(sketch);
        }
        {
            var Q0;
            Q0 = qSketchRegion(id + "F64", true);
            extrude(context, id + "F65", {"entities" : qUnion([Q0]), "operationType" : NewBodyOperationType.REMOVE, "endBound" : BoundingType.UP_TO_NEXT, "oppositeDirection" : true, "depth" : 25 * mm});
        }
        {
            var Q0;
            Q0=makeQuery(id+"F1.opExtrude","CAP_FACE",FACE,{"disambiguationData":[OSD([sQuery(id+"F0.wireOp",EDGE,"E0.bottom"),sQuery(id+"F0.wireOp",EDGE,"E0.top"),sQuery(id+"F0.wireOp",EDGE,"E0.left"),sQuery(id+"F0.wireOp",EDGE,"E0.right")])],"isStart":true});
            var sketch = newSketch(context, id + "F66", { "sketchPlane" : qUnion([Q0])});
            skLineSegment(sketch, "E309.bottom", {"start": v(16.75, 101.5) * mm, "end": v(165.25, 101.5) * mm});
            skLineSegment(sketch, "E309.top", {"start": v(16.75, 20) * mm, "end": v(165.25, 20) * mm});
            skLineSegment(sketch, "E309.left", {"start": v(16.75, 101.5) * mm, "end": v(16.75, 20) * mm});
            skLineSegment(sketch, "E309.right", {"start": v(165.25, 101.5) * mm, "end": v(165.25, 20) * mm});
            skSolve(sketch);
        }
        {
            var Q0;
            Q0 = qSketchRegion(id + "F66", true);
            extrude(context, id + "F67", {"entities" : qUnion([Q0]), "oppositeDirection" : true, "depth" : 140 * mm});
        }
        {
            var Q0;
            Q0=makeQuery(id+"F1.opExtrude","CAP_FACE",FACE,{"disambiguationData":[OSD([sQuery(id+"F0.wireOp",EDGE,"E0.bottom"),sQuery(id+"F0.wireOp",EDGE,"E0.top"),sQuery(id+"F0.wireOp",EDGE,"E0.left"),sQuery(id+"F0.wireOp",EDGE,"E0.right")])],"isStart":true});
            var sketch = newSketch(context, id + "F68", { "sketchPlane" : qUnion([Q0])});
            skLineSegment(sketch, "E310.bottom", {"start": v(16.75, 109.5) * mm, "end": v(119.2, 109.5) * mm});
            skLineSegment(sketch, "E310.top", {"start": v(16.75, 135) * mm, "end": v(119.2, 135) * mm});
            skLineSegment(sketch, "E310.left", {"start": v(16.75, 109.5) * mm, "end": v(16.75, 135) * mm});
            skLineSegment(sketch, "E310.right", {"start": v(119.2, 109.5) * mm, "end": v(119.2, 135) * mm});
            skLineSegment(sketch, "E311.bottom", {"start": v(19.25, 145) * mm, "end": v(89.25, 145) * mm});
            skLineSegment(sketch, "E311.top", {"start": v(19.25, 173.5) * mm, "end": v(89.25, 173.5) * mm});
            skLineSegment(sketch, "E311.left", {"start": v(19.25, 145) * mm, "end": v(19.25, 173.5) * mm});
            skLineSegment(sketch, "E311.right", {"start": v(89.25, 145) * mm, "end": v(89.25, 173.5) * mm});
            skLineSegment(sketch, "E312", {"start": v(54.25, 173.5) * mm, "end": v(54.25, 145) * mm, "construction": true});
            skLineSegment(sketch, "E313", {"start": v(67.98, 135) * mm, "end": v(67.98, 109.5) * mm, "construction": true});
            skSolve(sketch);
        }
        {
            var Q0;
            Q0 = qSketchRegion(id + "F68", true);
            extrude(context, id + "F69", {"entities" : qUnion([Q0]), "operationType" : NewBodyOperationType.REMOVE, "endBound" : BoundingType.UP_TO_NEXT, "oppositeDirection" : true, "depth" : 25 * mm});
        }
        {
            var Q0;
            Q0=makeQuery(id+"F1.opExtrude","CAP_FACE",FACE,{"disambiguationData":[OSD([sQuery(id+"F0.wireOp",EDGE,"E0.bottom"),sQuery(id+"F0.wireOp",EDGE,"E0.top"),sQuery(id+"F0.wireOp",EDGE,"E0.left"),sQuery(id+"F0.wireOp",EDGE,"E0.right")])],"isStart":true});
            var sketch = newSketch(context, id + "F70", { "sketchPlane" : qUnion([Q0])});
            skLineSegment(sketch, "E314.bottom", {"start": v(16.75, 109.5) * mm, "end": v(119.2, 109.5) * mm});
            skLineSegment(sketch, "E314.top", {"start": v(16.75, 135) * mm, "end": v(119.2, 135) * mm});
            skLineSegment(sketch, "E314.left", {"start": v(16.75, 109.5) * mm, "end": v(16.75, 135) * mm});
            skLineSegment(sketch, "E314.right", {"start": v(119.2, 109.5) * mm, "end": v(119.2, 135) * mm});
            skSolve(sketch);
        }
        {
            var Q0;
            Q0 = qSketchRegion(id + "F70", true);
            extrude(context, id + "F71", {"entities" : qUnion([Q0]), "oppositeDirection" : true, "depth" : 95.25 * mm});
        }
        {
            var Q0;
            Q0=makeQuery(id+"F1.opExtrude","CAP_FACE",FACE,{"disambiguationData":[OSD([sQuery(id+"F0.wireOp",EDGE,"E0.bottom"),sQuery(id+"F0.wireOp",EDGE,"E0.top"),sQuery(id+"F0.wireOp",EDGE,"E0.left"),sQuery(id+"F0.wireOp",EDGE,"E0.right")])],"isStart":true});
            var sketch = newSketch(context, id + "F72", { "sketchPlane" : qUnion([Q0])});
            skLineSegment(sketch, "E315.bottom", {"start": v(19.25, 173.5) * mm, "end": v(89.25, 173.5) * mm});
            skLineSegment(sketch, "E315.top", {"start": v(19.25, 145) * mm, "end": v(89.25, 145) * mm});
            skLineSegment(sketch, "E315.left", {"start": v(19.25, 173.5) * mm, "end": v(19.25, 145) * mm});
            skLineSegment(sketch, "E315.right", {"start": v(89.25, 173.5) * mm, "end": v(89.25, 145) * mm});
            skSolve(sketch);
        }
        {
            var Q0;
            Q0 = qSketchRegion(id + "F72", true);
            extrude(context, id + "F73", {"entities" : qUnion([Q0]), "oppositeDirection" : true, "depth" : 82 * mm});
        }
        {
            var Q0;
            Q0=makeQuery(id+"F73.opExtrude","CAP_FACE",FACE,{"disambiguationData":[OSD([sQuery(id+"F72.wireOp",EDGE,"E315.bottom"),sQuery(id+"F72.wireOp",EDGE,"E315.top"),sQuery(id+"F72.wireOp",EDGE,"E315.left"),sQuery(id+"F72.wireOp",EDGE,"E315.right")])],"isStart":true});
            var sketch = newSketch(context, id + "F74", { "sketchPlane" : qUnion([Q0])});
            skLineSegment(sketch, "E316.bottom", {"start": v(16.75, 176.48) * mm, "end": v(91.75, 176.48) * mm});
            skLineSegment(sketch, "E316.top", {"start": v(16.75, 142.03) * mm, "end": v(91.75, 142.03) * mm});
            skLineSegment(sketch, "E316.left", {"start": v(16.75, 176.48) * mm, "end": v(16.75, 142.03) * mm});
            skLineSegment(sketch, "E316.right", {"start": v(91.75, 176.48) * mm, "end": v(91.75, 142.03) * mm});
            skLineSegment(sketch, "E317", {"start": v(54.25, 173.5) * mm, "end": v(54.25, 229.44) * mm, "construction": true});
            skLineSegment(sketch, "E318", {"start": v(54.25, 176.48) * mm, "end": v(54.25, 150.21) * mm, "construction": true});
            skLineSegment(sketch, "E319", {"start": v(19.25, 159.25) * mm, "end": v(52.95, 159.25) * mm, "construction": true});
            skLineSegment(sketch, "E320", {"start": v(108, 159.25) * mm, "end": v(91.75, 159.25) * mm, "construction": true});
            skSolve(sketch);
        }
        {
            var Q0;
            Q0 = qSketchRegion(id + "F74", true);
            extrude(context, id + "F75", {"entities" : qUnion([Q0]), "operationType" : NewBodyOperationType.ADD, "depth" : 4 * mm});
        }
        {
            var Q0;
            Q0=makeQuery(id+"F75.opExtrude","CAP_EDGE",EDGE,{"disambiguationData":[OSD([sQuery(id+"F74.wireOp",EDGE,"E316.bottom")])],"isStart":false});
            var Q1;
            Q1=makeQuery(id+"F75.opExtrude","CAP_EDGE",EDGE,{"disambiguationData":[OSD([sQuery(id+"F74.wireOp",EDGE,"E316.top")])],"isStart":false});
            fillet(context, id + "F76", {"entities" : qUnion([Q0, Q1]), "radius" : 3 * mm, "tangentPropagation" : true, "allowEdgeOverflow" : false});
        }
        {
            var Q0;
            Q0=makeQuery(id+"F75.opExtrude","CAP_FACE",FACE,{"disambiguationData":[OSD([sQuery(id+"F74.wireOp",EDGE,"E316.bottom"),sQuery(id+"F74.wireOp",EDGE,"E316.top"),sQuery(id+"F74.wireOp",EDGE,"E316.left"),sQuery(id+"F74.wireOp",EDGE,"E316.right")])],"isStart":false});
            var sketch = newSketch(context, id + "F77", { "sketchPlane" : qUnion([Q0])});
            skLineSegment(sketch, "E321.bottom", {"start": v(26.75, 168.5) * mm, "end": v(66.75, 168.5) * mm});
            skLineSegment(sketch, "E321.top", {"start": v(26.75, 150) * mm, "end": v(66.75, 150) * mm});
            skLineSegment(sketch, "E321.left", {"start": v(26.75, 168.5) * mm, "end": v(26.75, 150) * mm});
            skLineSegment(sketch, "E321.right", {"start": v(66.75, 168.5) * mm, "end": v(66.75, 150) * mm});
            skLineSegment(sketch, "E322", {"start": v(26.75, 159.25) * mm, "end": v(52.37, 159.25) * mm, "construction": true});
            skLineSegment(sketch, "E323", {"start": v(18.59, 159.25) * mm, "end": v(16.75, 159.25) * mm, "construction": true});
            skSolve(sketch);
        }
        {
            var Q0;
            Q0 = qSketchRegion(id + "F77", true);
            extrude(context, id + "F78", {"entities" : qUnion([Q0]), "operationType" : NewBodyOperationType.REMOVE, "oppositeDirection" : true, "depth" : 0.1 * mm});
        }
        {
            var Q0;
            Q0=makeQuery(id+"F75.opExtrude","CAP_FACE",FACE,{"disambiguationData":[OSD([sQuery(id+"F74.wireOp",EDGE,"E316.bottom"),sQuery(id+"F74.wireOp",EDGE,"E316.top"),sQuery(id+"F74.wireOp",EDGE,"E316.left"),sQuery(id+"F74.wireOp",EDGE,"E316.right")])],"isStart":false});
            var sketch = newSketch(context, id + "F79", { "sketchPlane" : qUnion([Q0])});
            skLineSegment(sketch, "E324.bottom", {"start": v(71.75, 166) * mm, "end": v(77, 166) * mm});
            skLineSegment(sketch, "E324.top", {"start": v(71.75, 160.75) * mm, "end": v(77, 160.75) * mm});
            skLineSegment(sketch, "E324.left", {"start": v(71.75, 166) * mm, "end": v(71.75, 160.75) * mm});
            skLineSegment(sketch, "E324.right", {"start": v(77, 166) * mm, "end": v(77, 160.75) * mm});
            skLineSegment(sketch, "E325.bottom", {"start": v(80, 166) * mm, "end": v(85.25, 166) * mm});
            skLineSegment(sketch, "E325.top", {"start": v(80, 160.75) * mm, "end": v(85.25, 160.75) * mm});
            skLineSegment(sketch, "E325.left", {"start": v(80, 166) * mm, "end": v(80, 160.75) * mm});
            skLineSegment(sketch, "E325.right", {"start": v(85.25, 166) * mm, "end": v(85.25, 160.75) * mm});
            skLineSegment(sketch, "E326.bottom", {"start": v(80, 157.75) * mm, "end": v(85.25, 157.75) * mm});
            skLineSegment(sketch, "E326.top", {"start": v(80, 152.5) * mm, "end": v(85.25, 152.5) * mm});
            skLineSegment(sketch, "E326.left", {"start": v(80, 157.75) * mm, "end": v(80, 152.5) * mm});
            skLineSegment(sketch, "E326.right", {"start": v(85.25, 157.75) * mm, "end": v(85.25, 152.5) * mm});
            skLineSegment(sketch, "E327.bottom", {"start": v(71.75, 157.75) * mm, "end": v(77, 157.75) * mm});
            skLineSegment(sketch, "E327.top", {"start": v(71.75, 152.5) * mm, "end": v(77, 152.5) * mm});
            skLineSegment(sketch, "E327.left", {"start": v(71.75, 157.75) * mm, "end": v(71.75, 152.5) * mm});
            skLineSegment(sketch, "E327.right", {"start": v(77, 157.75) * mm, "end": v(77, 152.5) * mm});
            skLineSegment(sketch, "E328", {"start": v(77, 166) * mm, "end": v(80, 166) * mm, "construction": true});
            skLineSegment(sketch, "E329", {"start": v(85.25, 160.75) * mm, "end": v(85.25, 157.75) * mm, "construction": true});
            skLineSegment(sketch, "E330", {"start": v(85.25, 159.25) * mm, "end": v(108.1, 159.25) * mm, "construction": true});
            skLineSegment(sketch, "E331", {"start": v(70.6, 159.25) * mm, "end": v(66.75, 159.25) * mm, "construction": true});
            skSolve(sketch);
        }
        {
            var Q0;
            Q0 = qSketchRegion(id + "F79", true);
            extrude(context, id + "F80", {"entities" : qUnion([Q0]), "operationType" : NewBodyOperationType.ADD, "depth" : 1 * mm});
        }
        {
            var Q0;
            Q0=makeQuery(id+"F71.opExtrude","CAP_FACE",FACE,{"disambiguationData":[OSD([sQuery(id+"F70.wireOp",EDGE,"E314.bottom"),sQuery(id+"F70.wireOp",EDGE,"E314.top"),sQuery(id+"F70.wireOp",EDGE,"E314.left"),sQuery(id+"F70.wireOp",EDGE,"E314.right")])],"isStart":true});
            var sketch = newSketch(context, id + "F81", { "sketchPlane" : qUnion([Q0])});
            skLineSegment(sketch, "E332", {"start": v(16.75, 122.25) * mm, "end": v(35.35, 122.25) * mm, "construction": true});
            skLineSegment(sketch, "E333", {"start": v(35.35, 122.25) * mm, "end": v(57.1, 122.25) * mm, "construction": true});
            skLineSegment(sketch, "E334", {"start": v(57.1, 122.25) * mm, "end": v(78.85, 122.25) * mm, "construction": true});
            skLineSegment(sketch, "E335", {"start": v(78.85, 122.25) * mm, "end": v(100.6, 122.25) * mm, "construction": true});
            skLineSegment(sketch, "E336", {"start": v(100.6, 122.25) * mm, "end": v(119.2, 122.25) * mm, "construction": true});
            skCircle(sketch, "E337", {"center": v(35.35, 122.25) * mm, "radius": 6.42 * mm});
            skCircle(sketch, "E338", {"center": v(57.1, 122.25) * mm, "radius": 6.42 * mm});
            skCircle(sketch, "E339", {"center": v(78.85, 122.25) * mm, "radius": 6.42 * mm});
            skCircle(sketch, "E340", {"center": v(100.6, 122.25) * mm, "radius": 6.42 * mm});
            skSolve(sketch);
        }
        {
            var Q0;
            Q0 = qSketchRegion(id + "F81", true);
            extrude(context, id + "F82", {"entities" : qUnion([Q0]), "operationType" : NewBodyOperationType.ADD, "depth" : 10.5 * mm});
        }
        {
            var Q0;
            Q0=makeQuery(id+"F71.opExtrude","SWEPT_FACE",FACE,{"disambiguationData":[OSD([sQuery(id+"F70.wireOp",EDGE,"E314.left")])]});
            var sketch = newSketch(context, id + "F83", { "sketchPlane" : qUnion([Q0])});
            skLineSegment(sketch, "E341", {"start": v(0, 114) * mm, "end": v(-83.75, 114) * mm, "construction": true});
            skLineSegment(sketch, "E342", {"start": v(-83.75, 114) * mm, "end": v(-83.75, 109.5) * mm, "construction": true});
            skLineSegment(sketch, "E343", {"start": v(-23.5, 114) * mm, "end": v(-23.5, 109.5) * mm, "construction": true});
            skCircle(sketch, "E344", {"center": v(-83.75, 114) * mm, "radius": 0.72 * mm});
            skCircle(sketch, "E345", {"center": v(-23.5, 114) * mm, "radius": 0.72 * mm});
            skSolve(sketch);
        }
        {
            var Q0;
            Q0 = qSketchRegion(id + "F83", true);
            extrude(context, id + "F84", {"entities" : qUnion([Q0]), "operationType" : NewBodyOperationType.REMOVE, "endBound" : BoundingType.UP_TO_NEXT, "oppositeDirection" : true, "depth" : 25 * mm});
        }
        {
            var Q0;
            Q0=makeQuery(id+"F67.opExtrude","SWEPT_FACE",FACE,{"disambiguationData":[OSD([sQuery(id+"F66.wireOp",EDGE,"E309.bottom")])]});
            var sketch = newSketch(context, id + "F85", { "sketchPlane" : qUnion([Q0])});
            skLineSegment(sketch, "E346", {"start": v(165.25, 124.5) * mm, "end": v(141.25, 124.5) * mm, "construction": true});
            skLineSegment(sketch, "E347", {"start": v(141.25, 124.5) * mm, "end": v(141.25, 54) * mm, "construction": true});
            skLineSegment(sketch, "E348", {"start": v(141.25, 54) * mm, "end": v(165.25, 54) * mm, "construction": true});
            skLineSegment(sketch, "E349", {"start": v(165.25, 25) * mm, "end": v(130.25, 25) * mm, "construction": true});
            skLineSegment(sketch, "E350", {"start": v(130.25, 25) * mm, "end": v(130.25, 0) * mm, "construction": true});
            skCircle(sketch, "E351", {"center": v(130.25, 25) * mm, "radius": 6.35 * mm});
            skCircle(sketch, "E352", {"center": v(141.25, 54) * mm, "radius": 6.35 * mm});
            skCircle(sketch, "E353", {"center": v(141.25, 124.5) * mm, "radius": 6.35 * mm});
            skSolve(sketch);
        }
        {
            var Q0;
            Q0 = qSketchRegion(id + "F85", true);
            extrude(context, id + "F86", {"entities" : qUnion([Q0]), "operationType" : NewBodyOperationType.REMOVE, "oppositeDirection" : true, "depth" : 5 * mm});
        }
        {
            var Q0;
            Q0=makeQuery(id+"F86.boolean.opBoolean","COPY",FACE,{"derivedFrom":makeQuery(id+"F86.opExtrude","CAP_FACE",FACE,{"disambiguationData":[OSD([sQuery(id+"F85.wireOp",EDGE,"E351")])],"isStart":false})});
            var Q1;
            Q1=makeQuery(id+"F86.boolean.opBoolean","COPY",FACE,{"derivedFrom":makeQuery(id+"F86.opExtrude","CAP_FACE",FACE,{"disambiguationData":[OSD([sQuery(id+"F85.wireOp",EDGE,"E352")])],"isStart":false})});
            var Q2;
            Q2=makeQuery(id+"F86.boolean.opBoolean","COPY",FACE,{"derivedFrom":makeQuery(id+"F86.opExtrude","CAP_FACE",FACE,{"disambiguationData":[OSD([sQuery(id+"F85.wireOp",EDGE,"E353")])],"isStart":false})});
            shell(context, id + "F87", {"entities" : qUnion([Q0, Q1, Q2]), "thickness" : 5 * mm});
        }
        {
            var Q0;
            Q0=makeQuery(id+"F67.opExtrude","CAP_FACE",FACE,{"disambiguationData":[OSD([sQuery(id+"F66.wireOp",EDGE,"E309.bottom"),sQuery(id+"F66.wireOp",EDGE,"E309.top"),sQuery(id+"F66.wireOp",EDGE,"E309.left"),sQuery(id+"F66.wireOp",EDGE,"E309.right")])],"isStart":false});
            var sketch = newSketch(context, id + "F88", { "sketchPlane" : qUnion([Q0])});
            skLineSegment(sketch, "E354.bottom", {"start": v(-32.25, 36.5) * mm, "end": v(-70.25, 36.5) * mm});
            skLineSegment(sketch, "E354.top", {"start": v(-32.25, 74.5) * mm, "end": v(-70.25, 74.5) * mm});
            skLineSegment(sketch, "E354.left", {"start": v(-32.25, 36.5) * mm, "end": v(-32.25, 74.5) * mm});
            skLineSegment(sketch, "E354.right", {"start": v(-70.25, 36.5) * mm, "end": v(-70.25, 74.5) * mm});
            skSolve(sketch);
        }
        {
            var Q0;
            Q0 = qSketchRegion(id + "F88", true);
            extrude(context, id + "F89", {"entities" : qUnion([Q0]), "operationType" : NewBodyOperationType.REMOVE, "oppositeDirection" : true, "depth" : 5 * mm});
        }
        {
            var Q0;
            Q0=makeQuery(id+"F67.opExtrude","SWEPT_FACE",FACE,{"disambiguationData":[OSD([sQuery(id+"F66.wireOp",EDGE,"E309.left")])]});
            var sketch = newSketch(context, id + "F90", { "sketchPlane" : qUnion([Q0])});
            skLineSegment(sketch, "E355.bottom", {"start": v(-5, 20) * mm, "end": v(-140, 20) * mm});
            skLineSegment(sketch, "E355.top", {"start": v(-5, 101.5) * mm, "end": v(-140, 101.5) * mm});
            skLineSegment(sketch, "E355.left", {"start": v(-5, 20) * mm, "end": v(-5, 101.5) * mm});
            skLineSegment(sketch, "E355.right", {"start": v(-140, 20) * mm, "end": v(-140, 101.5) * mm});
            skSolve(sketch);
        }
        {
            var Q0;
            Q0 = qSketchRegion(id + "F90", true);
            extrude(context, id + "F91", {"entities" : qUnion([Q0]), "operationType" : NewBodyOperationType.REMOVE, "oppositeDirection" : true, "depth" : 2.5 * mm});
        }
        {
            var Q0;
            Q0=makeQuery(id+"F67.opExtrude","SWEPT_FACE",FACE,{"disambiguationData":[OSD([sQuery(id+"F66.wireOp",EDGE,"E309.right")])]});
            var sketch = newSketch(context, id + "F92", { "sketchPlane" : qUnion([Q0])});
            skLineSegment(sketch, "E356.bottom", {"start": v(5, 101.5) * mm, "end": v(140, 101.5) * mm});
            skLineSegment(sketch, "E356.top", {"start": v(5, 20) * mm, "end": v(140, 20) * mm});
            skLineSegment(sketch, "E356.left", {"start": v(5, 101.5) * mm, "end": v(5, 20) * mm});
            skLineSegment(sketch, "E356.right", {"start": v(140, 101.5) * mm, "end": v(140, 20) * mm});
            skSolve(sketch);
        }
        {
            var Q0;
            Q0 = qSketchRegion(id + "F92", true);
            extrude(context, id + "F93", {"entities" : qUnion([Q0]), "operationType" : NewBodyOperationType.REMOVE, "oppositeDirection" : true, "depth" : 1 * mm});
        }
        {
            var Q0;
            Q0=makeQuery(id+"F87.opShell","OFFSET_FACE",FACE,{"disambiguationData":[OSD([sQuery(id+"F66.wireOp",EDGE,"E309.right")])]});
            var sketch = newSketch(context, id + "F94", { "sketchPlane" : qUnion([Q0])});
            skLineSegment(sketch, "E357.0.0", {"start": v(-5, 25) * mm, "end": v(-5, 96.5) * mm});
            skLineSegment(sketch, "E357.0.1", {"start": v(-5, 96.5) * mm, "end": v(-135, 96.5) * mm});
            skLineSegment(sketch, "E357.0.2", {"start": v(-135, 96.5) * mm, "end": v(-135, 25) * mm});
            skLineSegment(sketch, "E357.0.3", {"start": v(-135, 25) * mm, "end": v(-5, 25) * mm});
            skSolve(sketch);
        }
        {
            var Q0;
            Q0 = qSketchRegion(id + "F94", true);
            extrude(context, id + "F95", {"entities" : qUnion([Q0]), "operationType" : NewBodyOperationType.ADD, "depth" : 6 * mm});
        }
        {
            var Q0;
            Q0=makeQuery(id+"F87.opShell","OFFSET_FACE",FACE,{"disambiguationData":[OSD([sQuery(id+"F66.wireOp",EDGE,"E309.left")])]});
            var sketch = newSketch(context, id + "F96", { "sketchPlane" : qUnion([Q0])});
            skLineSegment(sketch, "E358.0.0", {"start": v(5, 96.5) * mm, "end": v(5, 25) * mm});
            skLineSegment(sketch, "E358.0.1", {"start": v(5, 25) * mm, "end": v(135, 25) * mm});
            skLineSegment(sketch, "E358.0.2", {"start": v(135, 25) * mm, "end": v(135, 96.5) * mm});
            skLineSegment(sketch, "E358.0.3", {"start": v(135, 96.5) * mm, "end": v(5, 96.5) * mm});
            skSolve(sketch);
        }
        {
            var Q0;
            Q0 = qSketchRegion(id + "F96", true);
            extrude(context, id + "F97", {"entities" : qUnion([Q0]), "operationType" : NewBodyOperationType.ADD, "depth" : 7.5 * mm});
        }
        {
            var Q0;
            Q0=makeQuery(id+"F67.opExtrude","SWEPT_FACE",FACE,{"disambiguationData":[OSD([sQuery(id+"F66.wireOp",EDGE,"E309.bottom")])]});
            var sketch = newSketch(context, id + "F98", { "sketchPlane" : qUnion([Q0])});
            skLineSegment(sketch, "E359.bottom", {"start": v(31.5, 135) * mm, "end": v(91.5, 135) * mm});
            skLineSegment(sketch, "E359.top", {"start": v(31.5, 45) * mm, "end": v(91.5, 45) * mm});
            skLineSegment(sketch, "E359.left", {"start": v(31.5, 135) * mm, "end": v(31.5, 45) * mm});
            skLineSegment(sketch, "E359.right", {"start": v(91.5, 135) * mm, "end": v(91.5, 45) * mm});
            skSolve(sketch);
        }
        {
            var Q0;
            Q0 = qSketchRegion(id + "F98", true);
            extrude(context, id + "F99", {"entities" : qUnion([Q0]), "operationType" : NewBodyOperationType.REMOVE, "oppositeDirection" : true, "depth" : 5 * mm});
        }
        {
            var Q0;
            Q0=makeQuery(id+"F89.boolean.opBoolean","COPY",EDGE,{"derivedFrom":makeQuery(id+"F89.opExtrude","SWEPT_EDGE",EDGE,{"disambiguationData":[OSD([sQuery(id+"F88.wireOp",EDGE,"E354.bottom"),sQuery(id+"F88.wireOp",EDGE,"E354.right")])]})});
            var Q1;
            Q1=makeQuery(id+"F89.boolean.opBoolean","COPY",EDGE,{"derivedFrom":makeQuery(id+"F89.opExtrude","SWEPT_EDGE",EDGE,{"disambiguationData":[OSD([sQuery(id+"F88.wireOp",EDGE,"E354.bottom"),sQuery(id+"F88.wireOp",EDGE,"E354.left")])]})});
            var Q2;
            Q2=makeQuery(id+"F89.boolean.opBoolean","COPY",EDGE,{"derivedFrom":makeQuery(id+"F89.opExtrude","SWEPT_EDGE",EDGE,{"disambiguationData":[OSD([sQuery(id+"F88.wireOp",EDGE,"E354.top"),sQuery(id+"F88.wireOp",EDGE,"E354.left")])]})});
            var Q3;
            Q3=makeQuery(id+"F89.boolean.opBoolean","COPY",EDGE,{"derivedFrom":makeQuery(id+"F89.opExtrude","SWEPT_EDGE",EDGE,{"disambiguationData":[OSD([sQuery(id+"F88.wireOp",EDGE,"E354.top"),sQuery(id+"F88.wireOp",EDGE,"E354.right")])]})});
            var Q4;
            Q4=makeQuery(id+"F99.boolean.opBoolean","COPY",EDGE,{"derivedFrom":makeQuery(id+"F99.opExtrude","SWEPT_EDGE",EDGE,{"disambiguationData":[OSD([sQuery(id+"F98.wireOp",EDGE,"E359.top"),sQuery(id+"F98.wireOp",EDGE,"E359.right")])]})});
            var Q5;
            Q5=makeQuery(id+"F99.boolean.opBoolean","COPY",EDGE,{"derivedFrom":makeQuery(id+"F99.opExtrude","SWEPT_EDGE",EDGE,{"disambiguationData":[OSD([sQuery(id+"F98.wireOp",EDGE,"E359.top"),sQuery(id+"F98.wireOp",EDGE,"E359.left")])]})});
            fillet(context, id + "F100", {"entities" : qUnion([Q0, Q1, Q2, Q3, Q4, Q5]), "radius" : 4 * mm, "tangentPropagation" : true, "allowEdgeOverflow" : false});
        }
        {
            var Q0;
            Q0=makeQuery(id+"F87.opShell","OFFSET_FACE",FACE,{"disambiguationData":[OSD([sQuery(id+"F66.wireOp",EDGE,"E309.top")])]});
            var sketch = newSketch(context, id + "F101", { "sketchPlane" : qUnion([Q0])});
            skLineSegment(sketch, "E360.bottom", {"start": v(94.25, 135) * mm, "end": v(99.25, 135) * mm});
            skLineSegment(sketch, "E360.top", {"start": v(94.25, 5) * mm, "end": v(99.25, 5) * mm});
            skLineSegment(sketch, "E360.left", {"start": v(94.25, 135) * mm, "end": v(94.25, 5) * mm});
            skLineSegment(sketch, "E360.right", {"start": v(99.25, 135) * mm, "end": v(99.25, 5) * mm});
            skSolve(sketch);
        }
        {
            var Q0;
            Q0 = qSketchRegion(id + "F101", true);
            extrude(context, id + "F102", {"entities" : qUnion([Q0]), "operationType" : NewBodyOperationType.ADD, "endBound" : BoundingType.UP_TO_NEXT, "depth" : 25 * mm});
        }
        {
            var Q0;
            Q0=makeQuery(id+"F102.opExtrude","SWEPT_FACE",FACE,{"disambiguationData":[OSD([sQuery(id+"F101.wireOp",EDGE,"E360.left")])]});
            var sketch = newSketch(context, id + "F103", { "sketchPlane" : qUnion([Q0])});
            skLineSegment(sketch, "E361.bottom", {"start": v(-7.5, 50) * mm, "end": v(-14.5, 50) * mm});
            skLineSegment(sketch, "E361.top", {"start": v(-7.5, 59) * mm, "end": v(-14.5, 59) * mm});
            skLineSegment(sketch, "E361.left", {"start": v(-7.5, 50) * mm, "end": v(-7.5, 59) * mm});
            skLineSegment(sketch, "E361.right", {"start": v(-14.5, 50) * mm, "end": v(-14.5, 59) * mm});
            skSolve(sketch);
        }
        {
            var Q0;
            Q0 = qSketchRegion(id + "F103", true);
            extrude(context, id + "F104", {"entities" : qUnion([Q0]), "operationType" : NewBodyOperationType.REMOVE, "oppositeDirection" : true, "depth" : 5 * mm});
        }
        {
            var Q0;
            {var subQ0=sQuery(id+"F66.wireOp",EDGE,"E309.top");var subQ1=sQuery(id+"F66.wireOp",EDGE,"E309.bottom");var subQ2=sQuery(id+"F66.wireOp",EDGE,"E309.right");var subQ3=sQuery(id+"F66.wireOp",EDGE,"E309.left");Q0=makeQuery(id+"F102.boolean.opBoolean","SPLIT",FACE,{"disambiguationData":[TD([makeQuery(id+"F102.opExtrude","SWEPT_FACE",FACE,{"disambiguationData":[OSD([sQuery(id+"F101.wireOp",EDGE,"E360.left")])]})])],"derivedFrom":makeQuery(id+"F87.opShell","OFFSET_FACE",FACE,{"disambiguationData":[OSD([subQ1,subQ0,subQ3,subQ2]),TDD([makeQuery(id+"F67.opExtrude","CAP_FACE",FACE,{"disambiguationData":[OSD([subQ1,subQ0,subQ3,subQ2])],"isStart":true})])]})});}
            var sketch = newSketch(context, id + "F105", { "sketchPlane" : qUnion([Q0])});
            skLineSegment(sketch, "E362.bottom", {"start": v(-94.25, 59) * mm, "end": v(-29.25, 59) * mm});
            skLineSegment(sketch, "E362.top", {"start": v(-94.25, 64) * mm, "end": v(-29.25, 64) * mm});
            skLineSegment(sketch, "E362.left", {"start": v(-94.25, 59) * mm, "end": v(-94.25, 64) * mm});
            skLineSegment(sketch, "E362.right", {"start": v(-29.25, 59) * mm, "end": v(-29.25, 64) * mm});
            skSolve(sketch);
        }
        {
            var Q0;
            Q0 = qSketchRegion(id + "F105", true);
            extrude(context, id + "F106", {"entities" : qUnion([Q0]), "operationType" : NewBodyOperationType.ADD, "depth" : 76.5 * mm});
        }
        {
            var Q0;
            Q0=makeQuery(id+"F106.opExtrude","CAP_FACE",FACE,{"disambiguationData":[OSD([sQuery(id+"F105.wireOp",EDGE,"E362.bottom"),sQuery(id+"F105.wireOp",EDGE,"E362.top"),sQuery(id+"F105.wireOp",EDGE,"E362.left"),sQuery(id+"F105.wireOp",EDGE,"E362.right")])],"isStart":false});
            var sketch = newSketch(context, id + "F107", { "sketchPlane" : qUnion([Q0])});
            skLineSegment(sketch, "E363.bottom", {"start": v(-94.25, 64) * mm, "end": v(-29.25, 64) * mm});
            skLineSegment(sketch, "E363.top", {"start": v(-94.25, 25) * mm, "end": v(-71.75, 25) * mm});
            skLineSegment(sketch, "E363.left", {"start": v(-94.25, 64) * mm, "end": v(-94.25, 25) * mm});
            skLineSegment(sketch, "E363.right", {"start": v(-29.25, 64) * mm, "end": v(-29.25, 25) * mm});
            skLineSegment(sketch, "E364", {"start": v(-61.75, 25) * mm, "end": v(-61.75, 35) * mm, "construction": true});
            skLineSegment(sketch, "E365.top", {"start": v(-71.75, 31) * mm, "end": v(-51.75, 31) * mm});
            skLineSegment(sketch, "E365.left", {"start": v(-71.75, 25) * mm, "end": v(-71.75, 31) * mm});
            skLineSegment(sketch, "E365.right", {"start": v(-51.75, 25) * mm, "end": v(-51.75, 31) * mm});
            skLineSegment(sketch, "E366", {"start": v(-61.75, 40.59) * mm, "end": v(-61.75, 31) * mm, "construction": true});
            skLineSegment(sketch, "E367.trimOffspring", {"start": v(-51.75, 25) * mm, "end": v(-29.25, 25) * mm});
            skSolve(sketch);
        }
        {
            var Q0;
            Q0 = qSketchRegion(id + "F107", true);
            extrude(context, id + "F108", {"entities" : qUnion([Q0]), "operationType" : NewBodyOperationType.ADD, "oppositeDirection" : true, "depth" : 5 * mm});
        }
        {
            var Q0;
            {var subQ2=sQuery(id+"F66.wireOp",EDGE,"E309.top");Q0=makeQuery(id+"F102.boolean.opBoolean","SPLIT",FACE,{"disambiguationData":[TD([makeQuery(id+"F102.opExtrude","SWEPT_FACE",FACE,{"disambiguationData":[OSD([sQuery(id+"F101.wireOp",EDGE,"E360.left")])]})])],"derivedFrom":makeQuery(id+"F87.opShell","OFFSET_FACE",FACE,{"disambiguationData":[OSD([subQ2])]})});}
            var sketch = newSketch(context, id + "F109", { "sketchPlane" : qUnion([Q0])});
            skLineSegment(sketch, "E368.bottom", {"start": v(94.25, 20.5) * mm, "end": v(66.75, 20.5) * mm});
            skLineSegment(sketch, "E368.top", {"start": v(94.25, 25.5) * mm, "end": v(66.75, 25.5) * mm});
            skLineSegment(sketch, "E368.left", {"start": v(94.25, 20.5) * mm, "end": v(94.25, 25.5) * mm});
            skLineSegment(sketch, "E368.right", {"start": v(66.75, 20.5) * mm, "end": v(66.75, 25.5) * mm});
            skSolve(sketch);
        }
        {
            var Q0;
            Q0 = qSketchRegion(id + "F109", true);
            extrude(context, id + "F110", {"entities" : qUnion([Q0]), "operationType" : NewBodyOperationType.ADD, "endBound" : BoundingType.UP_TO_NEXT, "depth" : 25 * mm});
        }
        {
            var Q0;
            Q0=makeQuery(id+"F67.opExtrude","CAP_FACE",FACE,{"disambiguationData":[OSD([sQuery(id+"F66.wireOp",EDGE,"E309.bottom"),sQuery(id+"F66.wireOp",EDGE,"E309.top"),sQuery(id+"F66.wireOp",EDGE,"E309.left"),sQuery(id+"F66.wireOp",EDGE,"E309.right")])],"isStart":false});
            var sketch = newSketch(context, id + "F111", { "sketchPlane" : qUnion([Q0])});
            skLineSegment(sketch, "E369", {"start": v(-108.75, 101.5) * mm, "end": v(-108.75, 51.5) * mm, "construction": true});
            skLineSegment(sketch, "E370", {"start": v(-108.75, 51.5) * mm, "end": v(-164.25, 51.5) * mm, "construction": true});
            skLineSegment(sketch, "E371", {"start": v(-108.75, 83.5) * mm, "end": v(-164.25, 83.5) * mm, "construction": true});
            skCircle(sketch, "E372", {"center": v(-108.75, 83.5) * mm, "radius": 6.35 * mm});
            skCircle(sketch, "E373", {"center": v(-108.75, 51.5) * mm, "radius": 6.35 * mm});
            skSolve(sketch);
        }
        {
            var Q0;
            Q0 = qSketchRegion(id + "F111", true);
            extrude(context, id + "F112", {"entities" : qUnion([Q0]), "operationType" : NewBodyOperationType.REMOVE, "endBound" : BoundingType.UP_TO_NEXT, "oppositeDirection" : true, "depth" : 25 * mm});
        }
        {
            var Q0;
            {var subQ2=sQuery(id+"F66.wireOp",EDGE,"E309.top");Q0=makeQuery(id+"F102.boolean.opBoolean","SPLIT",FACE,{"disambiguationData":[TD([makeQuery(id+"F102.opExtrude","SWEPT_FACE",FACE,{"disambiguationData":[OSD([sQuery(id+"F101.wireOp",EDGE,"E360.left")])]})])],"derivedFrom":makeQuery(id+"F87.opShell","OFFSET_FACE",FACE,{"disambiguationData":[OSD([subQ2])]})});}
            var sketch = newSketch(context, id + "F113", { "sketchPlane" : qUnion([Q0])});
            skLineSegment(sketch, "E374.bottom", {"start": v(36.75, 81.5) * mm, "end": v(51.75, 81.5) * mm});
            skLineSegment(sketch, "E374.top", {"start": v(36.75, 135) * mm, "end": v(88.25, 135) * mm});
            skLineSegment(sketch, "E374.left", {"start": v(36.75, 81.5) * mm, "end": v(36.75, 135) * mm});
            skLineSegment(sketch, "E374.right", {"start": v(88.25, 81.5) * mm, "end": v(88.25, 135) * mm});
            skLineSegment(sketch, "E375.left", {"start": v(71.75, 81.5) * mm, "end": v(71.75, 107.75) * mm});
            skLineSegment(sketch, "E375.right", {"start": v(51.75, 81.5) * mm, "end": v(51.75, 107.75) * mm});
            skArc(sketch, "E376", {"start": v(71.75, 107.75) * mm, "mid": v(61.75, 117.75) * mm, "end": v(51.75, 107.75) * mm});
            skLineSegment(sketch, "E377.trimOffspring", {"start": v(71.75, 81.5) * mm, "end": v(88.25, 81.5) * mm});
            skSolve(sketch);
        }
        {
            var Q0;
            Q0 = qSketchRegion(id + "F113", true);
            extrude(context, id + "F114", {"entities" : qUnion([Q0]), "operationType" : NewBodyOperationType.ADD, "depth" : 6 * mm});
        }
        {
            var Q0;
            Q0=makeQuery(id+"F114.opExtrude","CAP_FACE",FACE,{"disambiguationData":[OSD([sQuery(id+"F113.wireOp",EDGE,"E374.bottom"),sQuery(id+"F113.wireOp",EDGE,"E374.top"),sQuery(id+"F113.wireOp",EDGE,"E374.left"),sQuery(id+"F113.wireOp",EDGE,"E374.right"),sQuery(id+"F113.wireOp",EDGE,"E375.left"),sQuery(id+"F113.wireOp",EDGE,"E375.right"),sQuery(id+"F113.wireOp",EDGE,"E376"),sQuery(id+"F113.wireOp",EDGE,"E377.trimOffspring")])],"isStart":false});
            var sketch = newSketch(context, id + "F115", { "sketchPlane" : qUnion([Q0])});
            skLineSegment(sketch, "E378.bottom", {"start": v(88.25, 81.5) * mm, "end": v(36.75, 81.5) * mm});
            skLineSegment(sketch, "E378.top", {"start": v(88.25, 135) * mm, "end": v(36.75, 135) * mm});
            skLineSegment(sketch, "E378.left", {"start": v(88.25, 81.5) * mm, "end": v(88.25, 135) * mm});
            skLineSegment(sketch, "E378.right", {"start": v(36.75, 81.5) * mm, "end": v(36.75, 135) * mm});
            skCircle(sketch, "E379", {"center": v(61.75, 107.75) * mm, "radius": 10 * mm});
            skSolve(sketch);
        }
        {
            var Q0;
            Q0 = qSketchRegion(id + "F115", true);
            extrude(context, id + "F116", {"entities" : qUnion([Q0]), "operationType" : NewBodyOperationType.ADD, "depth" : 6 * mm});
        }
        {
            var Q0;
            Q0=makeQuery(id+"F19.opPattern","COPY",FACE,{"derivedFrom":makeQuery(id+"F1.opExtrude","CAP_FACE",FACE,{"disambiguationData":[OSD([sQuery(id+"F0.wireOp",EDGE,"E0.bottom"),sQuery(id+"F0.wireOp",EDGE,"E0.top"),sQuery(id+"F0.wireOp",EDGE,"E0.left"),sQuery(id+"F0.wireOp",EDGE,"E0.right")])],"isStart":false}),"instanceName":"1"});
            var sketch = newSketch(context, id + "F117", { "sketchPlane" : qUnion([Q0])});
            skLineSegment(sketch, "E380.0", {"start": v(74.5, 312.5) * mm, "end": v(10, 312.5) * mm, "construction": true});
            skLineSegment(sketch, "E381.0", {"start": v(74.5, 114) * mm, "end": v(74.5, 312.5) * mm, "construction": true});
            skLineSegment(sketch, "E382.0", {"start": v(10, 312.5) * mm, "end": v(10, 0) * mm, "construction": true});
            skPoint(sketch, "E383.orphan", {"position": v(10, 332.5) * mm});
            skPoint(sketch, "E384.orphan", {"position": v(172, 312.5) * mm});
            skLineSegment(sketch, "E385", {"start": v(42.25, 312.5) * mm, "end": v(42.25, 291.07) * mm, "construction": true});
            skLineSegment(sketch, "E386", {"start": v(42.25, 291.07) * mm, "end": v(10, 291.07) * mm, "construction": true});
            skCircle(sketch, "E387", {"center": v(42.25, 291.07) * mm, "radius": 21 * mm});
            skSolve(sketch);
        }
        {
            var Q0;
            Q0 = qSketchRegion(id + "F117", true);
            extrude(context, id + "F118", {"entities" : qUnion([Q0]), "operationType" : NewBodyOperationType.REMOVE, "endBound" : BoundingType.UP_TO_NEXT, "oppositeDirection" : true, "depth" : 25 * mm});
        }
        {
            var Q0;
            Q0=makeQuery(id+"F19.opPattern","COPY",FACE,{"derivedFrom":makeQuery(id+"F1.opExtrude","CAP_FACE",FACE,{"disambiguationData":[OSD([sQuery(id+"F0.wireOp",EDGE,"E0.bottom"),sQuery(id+"F0.wireOp",EDGE,"E0.top"),sQuery(id+"F0.wireOp",EDGE,"E0.left"),sQuery(id+"F0.wireOp",EDGE,"E0.right")])],"isStart":true}),"instanceName":"1"});
            var sketch = newSketch(context, id + "F119", { "sketchPlane" : qUnion([Q0])});
            skCircle(sketch, "E388", {"center": v(-42.25, 291.07) * mm, "radius": 16 * mm});
            skCircle(sketch, "E389.0", {"center": v(-42.25, 291.07) * mm, "radius": 21 * mm});
            skSolve(sketch);
        }
        {
            var Q0;
            Q0 = qSketchRegion(id + "F119", true);
            extrude(context, id + "F120", {"entities" : qUnion([Q0]), "oppositeDirection" : true, "depth" : 55 * mm});
        }
        {
            var Q0;
            Q0=makeQuery(id+"F120.opExtrude","CAP_FACE",FACE,{"disambiguationData":[OSD([sQuery(id+"F119.wireOp",EDGE,"E388"),sQuery(id+"F119.wireOp",EDGE,"E389.0")])],"isStart":true});
            var sketch = newSketch(context, id + "F121", { "sketchPlane" : qUnion([Q0])});
            skCircle(sketch, "E390", {"center": v(-42.25, 291.07) * mm, "radius": 33 * mm});
            skCircle(sketch, "E391.0", {"center": v(-42.25, 291.07) * mm, "radius": 16 * mm});
            skCircle(sketch, "E392", {"center": v(-42.25, 291.07) * mm, "radius": 27 * mm, "construction": true});
            skLineSegment(sketch, "E393", {"start": v(-42.25, 291.07) * mm, "end": v(-42.25, 318.07) * mm, "construction": true});
            skLineSegment(sketch, "E394", {"start": v(-42.25, 291.07) * mm, "end": v(-15.25, 291.07) * mm, "construction": true});
            skLineSegment(sketch, "E395", {"start": v(-42.25, 291.07) * mm, "end": v(-42.25, 264.07) * mm, "construction": true});
            skLineSegment(sketch, "E396", {"start": v(-42.25, 291.07) * mm, "end": v(-69.25, 291.07) * mm, "construction": true});
            skLineSegment(sketch, "E397", {"start": v(-42.25, 291.07) * mm, "end": v(-23.16, 310.17) * mm, "construction": true});
            skLineSegment(sketch, "E398", {"start": v(-42.25, 291.07) * mm, "end": v(-61.34, 310.17) * mm, "construction": true});
            skLineSegment(sketch, "E399", {"start": v(-42.25, 291.07) * mm, "end": v(-61.34, 271.98) * mm, "construction": true});
            skLineSegment(sketch, "E400", {"start": v(-42.25, 291.07) * mm, "end": v(-23.16, 271.98) * mm, "construction": true});
            skCircle(sketch, "E401", {"center": v(-23.16, 310.17) * mm, "radius": 1.5 * mm});
            skCircle(sketch, "E402", {"center": v(-15.25, 291.07) * mm, "radius": 1.5 * mm});
            skCircle(sketch, "E403", {"center": v(-23.16, 271.98) * mm, "radius": 1.5 * mm});
            skCircle(sketch, "E404", {"center": v(-42.25, 264.07) * mm, "radius": 1.5 * mm});
            skCircle(sketch, "E405", {"center": v(-61.34, 271.98) * mm, "radius": 1.5 * mm});
            skCircle(sketch, "E406", {"center": v(-69.25, 291.07) * mm, "radius": 1.5 * mm});
            skCircle(sketch, "E407", {"center": v(-61.34, 310.17) * mm, "radius": 1.5 * mm});
            skCircle(sketch, "E408", {"center": v(-42.25, 318.07) * mm, "radius": 1.5 * mm});
            skSolve(sketch);
        }
        {
            var Q0;
            Q0 = qSketchRegion(id + "F121", true);
            extrude(context, id + "F122", {"entities" : qUnion([Q0]), "operationType" : NewBodyOperationType.ADD, "depth" : 5 * mm});
        }
        {
            var Q0;
            Q0=makeQuery(id+"F122.opExtrude","CAP_EDGE",EDGE,{"disambiguationData":[OSD([sQuery(id+"F121.wireOp",EDGE,"E390")])],"isStart":false});
            chamfer(context, id + "F123", {"entities" : qUnion([Q0]), "width" : 2.5 * mm, "tangentPropagation" : true});
        }
        {
            var Q0;
            Q0=makeQuery(id+"F19.opPattern","COPY",FACE,{"derivedFrom":makeQuery(id+"F1.opExtrude","CAP_FACE",FACE,{"disambiguationData":[OSD([sQuery(id+"F0.wireOp",EDGE,"E0.bottom"),sQuery(id+"F0.wireOp",EDGE,"E0.top"),sQuery(id+"F0.wireOp",EDGE,"E0.left"),sQuery(id+"F0.wireOp",EDGE,"E0.right")])],"isStart":true}),"instanceName":"1"});
            var sketch = newSketch(context, id + "F124", { "sketchPlane" : qUnion([Q0])});
            skCircle(sketch, "E409.0", {"center": v(-42.25, 318.07) * mm, "radius": 1.5 * mm});
            skCircle(sketch, "E409.1", {"center": v(-23.16, 310.17) * mm, "radius": 1.5 * mm});
            skCircle(sketch, "E409.2", {"center": v(-15.25, 291.07) * mm, "radius": 1.5 * mm});
            skCircle(sketch, "E409.3", {"center": v(-23.16, 271.98) * mm, "radius": 1.5 * mm});
            skCircle(sketch, "E409.4", {"center": v(-42.25, 264.07) * mm, "radius": 1.5 * mm});
            skCircle(sketch, "E409.5", {"center": v(-61.34, 271.98) * mm, "radius": 1.5 * mm});
            skCircle(sketch, "E409.6", {"center": v(-69.25, 291.07) * mm, "radius": 1.5 * mm});
            skCircle(sketch, "E409.7", {"center": v(-61.34, 310.17) * mm, "radius": 1.5 * mm});
            skSolve(sketch);
        }
        {
            var Q0;
            Q0 = qSketchRegion(id + "F124", true);
            extrude(context, id + "F125", {"entities" : qUnion([Q0]), "operationType" : NewBodyOperationType.REMOVE, "endBound" : BoundingType.UP_TO_NEXT, "oppositeDirection" : true, "depth" : 25 * mm});
        }
        {
            var Q0;
            Q0=makeQuery(id+"F21.opExtrude","CAP_FACE",FACE,{"disambiguationData":[OSD([sQuery(id+"F20.wireOp",EDGE,"E141.bottom"),sQuery(id+"F20.wireOp",EDGE,"E141.top"),sQuery(id+"F20.wireOp",EDGE,"E141.left"),sQuery(id+"F20.wireOp",EDGE,"E141.right"),sQuery(id+"F20.wireOp",EDGE,"E142.filletArc"),sQuery(id+"F20.wireOp",EDGE,"E143.filletArc"),sQuery(id+"F20.wireOp",EDGE,"E144.filletArc"),sQuery(id+"F20.wireOp",EDGE,"E145.filletArc"),sQuery(id+"F20.wireOp",EDGE,"E148"),sQuery(id+"F20.wireOp",EDGE,"E149"),sQuery(id+"F20.wireOp",EDGE,"E150"),sQuery(id+"F20.wireOp",EDGE,"E151"),sQuery(id+"F20.wireOp",EDGE,"E152"),sQuery(id+"F20.wireOp",EDGE,"E153"),sQuery(id+"F20.wireOp",EDGE,"E154"),sQuery(id+"F20.wireOp",EDGE,"E155"),sQuery(id+"F20.wireOp",EDGE,"E156"),sQuery(id+"F20.wireOp",EDGE,"E157"),sQuery(id+"F20.wireOp",EDGE,"E158"),sQuery(id+"F20.wireOp",EDGE,"E159"),sQuery(id+"F20.wireOp",EDGE,"E160"),sQuery(id+"F20.wireOp",EDGE,"E161"),sQuery(id+"F20.wireOp",EDGE,"E162"),sQuery(id+"F20.wireOp",EDGE,"E163"),sQuery(id+"F20.wireOp",EDGE,"E164"),sQuery(id+"F20.wireOp",EDGE,"E165"),sQuery(id+"F20.wireOp",EDGE,"E172"),sQuery(id+"F20.wireOp",EDGE,"E173")])],"isStart":true});
            var sketch = newSketch(context, id + "F126", { "sketchPlane" : qUnion([Q0])});
            skCircle(sketch, "E410.0", {"center": v(141.25, -54) * mm, "radius": 6.35 * mm});
            skSolve(sketch);
        }
        {
            var Q0;
            Q0 = qSketchRegion(id + "F126", true);
            extrude(context, id + "F127", {"entities" : qUnion([Q0]), "operationType" : NewBodyOperationType.REMOVE, "endBound" : BoundingType.UP_TO_NEXT, "oppositeDirection" : true, "depth" : 25 * mm});
        }
        {
            var Q0;
            Q0=makeQuery(id+"F18.opPattern","COPY",FACE,{"derivedFrom":makeQuery(id+"F16.opPattern","COPY",FACE,{"derivedFrom":makeQuery(id+"F12.opExtrude","SWEPT_FACE",FACE,{"disambiguationData":[OSD([sQuery(id+"F7.wireOp",EDGE,"E128.trimOffspring")])]}),"instanceName":"1"}),"instanceName":"1"});
            var sketch = newSketch(context, id + "F128", { "sketchPlane" : qUnion([Q0])});
            skLineSegment(sketch, "E411.bottom", {"start": v(-6, -361) * mm, "end": v(188, -361) * mm});
            skLineSegment(sketch, "E411.top", {"start": v(-6, -291) * mm, "end": v(188, -291) * mm});
            skLineSegment(sketch, "E411.left", {"start": v(-6, -361) * mm, "end": v(-6, -291) * mm});
            skLineSegment(sketch, "E411.right", {"start": v(188, -361) * mm, "end": v(188, -291) * mm});
            skLineSegment(sketch, "E412", {"start": v(4, -291) * mm, "end": v(4, -361) * mm, "construction": true});
            skLineSegment(sketch, "E413", {"start": v(178, -291) * mm, "end": v(178, -361) * mm, "construction": true});
            skLineSegment(sketch, "E414", {"start": v(4, -307.96) * mm, "end": v(178, -307.96) * mm, "construction": true});
            skLineSegment(sketch, "E415", {"start": v(4, -346.66) * mm, "end": v(178, -346.66) * mm, "construction": true});
            skCircle(sketch, "E416", {"center": v(4, -307.96) * mm, "radius": 2 * mm});
            skCircle(sketch, "E417", {"center": v(4, -346.66) * mm, "radius": 2 * mm});
            skCircle(sketch, "E418", {"center": v(178, -346.66) * mm, "radius": 2 * mm});
            skCircle(sketch, "E419", {"center": v(178, -307.96) * mm, "radius": 2 * mm});
            skSolve(sketch);
        }
        {
            var Q0;
            Q0 = qSketchRegion(id + "F128", true);
            extrude(context, id + "F129", {"entities" : qUnion([Q0]), "depth" : 5 * mm});
        }
    });
